FREECAD ASSEMBLY — COMPONENT RECIPES ("proj2")

This assembly document has 16 components, labeled P0..P15 below (a component is one placed body or linked part). 15 of them carry a construction recipe — the FreeCAD feature program that regenerates the part from scratch, quoted from this document or its linked companion documents; the rest are supplied as boundary geometry only. No exploded tour is included for this assembly.
COMPONENT P0 — geometry summary ("Assembly"; no construction recipe available for this part):
  bounding box: 60.6 x 47.8 x 42.0 mm
  tessellated surface: 6,332 triangles
  volume: 119726214130147568963238807791653928811536405446377303989115812334621021626623820741472012231102444157712454609502401804820784934384684739682024730656768 mm^3 (98328918981775611600278971227249126254820471256093482078634739637553224683712798080618531052465940639860308786772171943274562947930039704154529595392% of its bounding box)
COMPONENT P1 — recipe-attached ("classifier", modeled in this document).
Construction recipe (the document's own serialized feature program — sketch geometry with constraints, then the solid features built on it; lengths are millimeters unless a unit is written):

FEATURE [Sketcher::SketchObject] Sketch
  FullyConstrained = true
  MapMode = 5
  sketch-geometry (38):
    g0: LineSegment StartX=0 StartY=100 StartZ=0 EndX=0 EndY=200 EndZ=0
    g1: LineSegment StartX=0 StartY=200 StartZ=0 EndX=-86.6025 EndY=250 EndZ=0
    g2: LineSegment StartX=-86.6025 StartY=250 StartZ=0 EndX=-173.205 EndY=200 EndZ=0
    g3: LineSegment StartX=-173.205 StartY=200 StartZ=0 EndX=-173.205 EndY=100 EndZ=0
    g4: LineSegment StartX=-173.205 StartY=100 StartZ=0 EndX=-86.6025 EndY=50 EndZ=0
    g5: LineSegment StartX=-86.6025 StartY=50 StartZ=0 EndX=0 EndY=100 EndZ=0
    g6: Circle CenterX=-86.6025 CenterY=150 CenterZ=0 NormalX=0 NormalY=0 NormalZ=1 AngleXU=0 Radius=100
    g7: LineSegment StartX=173.205 StartY=100 StartZ=0 EndX=173.205 EndY=200 EndZ=0
    g8: LineSegment StartX=0 StartY=100 StartZ=0 EndX=86.6025 EndY=50 EndZ=0
    g9: LineSegment StartX=86.6025 StartY=50 StartZ=0 EndX=173.205 EndY=100 EndZ=0
    g10: LineSegment StartX=173.205 StartY=200 StartZ=0 EndX=86.6025 EndY=250 EndZ=0
    g11: LineSegment StartX=86.6025 StartY=250 StartZ=0 EndX=0 EndY=200 EndZ=0
    g12: Circle CenterX=86.6025 CenterY=150 CenterZ=0 NormalX=0 NormalY=0 NormalZ=1 AngleXU=0 Radius=100
    g13: LineSegment StartX=86.6025 StartY=-50 StartZ=0 EndX=86.6025 EndY=50 EndZ=0
    g14: LineSegment StartX=259.808 StartY=-50 StartZ=0 EndX=259.808 EndY=50 EndZ=0
    g15: LineSegment StartX=86.6025 StartY=-50 StartZ=0 EndX=173.205 EndY=-100 EndZ=0
    g16: LineSegment StartX=173.205 StartY=-100 StartZ=0 EndX=259.808 EndY=-50 EndZ=0
    g17: LineSegment StartX=259.808 StartY=50 StartZ=0 EndX=173.205 EndY=100 EndZ=0
    g18: Circle CenterX=173.205 CenterY=1e-16 CenterZ=0 NormalX=0 NormalY=0 NormalZ=1 AngleXU=0 Radius=100
    g19: LineSegment StartX=1.17e-14 StartY=-100 StartZ=0 EndX=86.6025 EndY=-50 EndZ=0
    g20: LineSegment StartX=86.6025 StartY=-250 StartZ=0 EndX=173.205 EndY=-200 EndZ=0
    g21: LineSegment StartX=1.76e-14 StartY=-200 StartZ=0 EndX=86.6025 EndY=-250 EndZ=0
    g22: LineSegment StartX=173.205 StartY=-200 StartZ=0 EndX=173.205 EndY=-100 EndZ=0
    g23: Circle CenterX=86.6025 CenterY=-150 CenterZ=0 NormalX=0 NormalY=0 NormalZ=1 AngleXU=0 Radius=100
    g24: LineSegment StartX=-86.6025 StartY=-50 StartZ=0 EndX=-86.6025 EndY=50 EndZ=0
    g25: LineSegment StartX=-173.205 StartY=100 StartZ=0 EndX=-259.808 EndY=50 EndZ=0
    g26: LineSegment StartX=-259.808 StartY=50 StartZ=0 EndX=-259.808 EndY=-50 EndZ=0
    g27: LineSegment StartX=-259.808 StartY=-50 StartZ=0 EndX=-173.205 EndY=-100 EndZ=0
    g28: LineSegment StartX=-173.205 StartY=-100 StartZ=0 EndX=-86.6025 EndY=-50 EndZ=0
    g29: Circle CenterX=-173.205 CenterY=-1.25e-14 CenterZ=0 NormalX=0 NormalY=0 NormalZ=1 AngleXU=0 Radius=100
    g30: LineSegment StartX=0 StartY=-200 StartZ=0 EndX=1.17e-14 EndY=-100 EndZ=0
    g31: LineSegment StartX=1.17e-14 StartY=-100 StartZ=0 EndX=-86.6025 EndY=-50 EndZ=0
    g32: LineSegment StartX=-173.205 StartY=-100 StartZ=0 EndX=-173.205 EndY=-200 EndZ=0
    g33: LineSegment StartX=-173.205 StartY=-200 StartZ=0 EndX=-86.6025 EndY=-250 EndZ=0
    g34: LineSegment StartX=-86.6025 StartY=-250 StartZ=0 EndX=0 EndY=-200 EndZ=0
    g35: Circle CenterX=-86.6025 CenterY=-150 CenterZ=0 NormalX=0 NormalY=0 NormalZ=1 AngleXU=0 Radius=100
    g36: GeomPoint X=86.6025 Y=150 Z=0
    g37: GeomPoint X=86.6025 Y=150 Z=0
  constraints (94):
    c: Coincident(g0,g1)
    c: Coincident(g1,g2)
    c: Coincident(g2,g3)
    c: Coincident(g3,g4)
    c: Coincident(g4,g5)
    c: Coincident(g5,g0)
    c: Equal(g0, g1-g5) x5
    c: PointOnObject(g0,g6)
    c: PointOnObject(g1,g6)
    c: PointOnObject(g2,g6)
    c: PointOnObject(g3,g6)
    c: PointOnObject(g4,g6)
    c: PointOnObject(g5,g6)
    c: Tangent(g0,g-2)
    c: DistanceY(g0,g0) = 100
    c: Coincident(g7,g10)
    c: Coincident(g10,g11)
    c: Coincident(g8,g9)
    c: Coincident(g9,g7)
    c: Equal(g7,g10)
    c: Equal(g7,g11)
    c: Equal(g7,g8)
    c: Equal(g7,g9)
    c: PointOnObject(g7,g12)
    c: PointOnObject(g10,g12)
    c: PointOnObject(g11,g12)
    c: PointOnObject(g8,g12)
    c: PointOnObject(g8,g12)
    c: PointOnObject(g9,g12)
    c: Equal(g0,g7) = 100
    c: Coincident(g11,g0)
    c: Coincident(g8,g0)
    c: Equal(g0,g13) = 100
    c: Coincident(g14,g17)
    c: Coincident(g15,g16)
    c: Coincident(g16,g14)
    c: Equal(g14,g17)
    c: Equal(g14,g15)
    c: Equal(g14,g16)
    c: PointOnObject(g14,g18)
    c: PointOnObject(g17,g18)
    c: PointOnObject(g13,g18)
    c: PointOnObject(g15,g18)
    c: PointOnObject(g15,g18)
    c: PointOnObject(g16,g18)
    c: Equal(g13,g14) = 100
    c: Coincident(g15,g13)
    c: Coincident(g17,g7)
    c: Coincident(g13,g8)
    c: Coincident(g20,g22)
    c: Coincident(g21,g20)
    c: Equal(g20,g22)
    c: Equal(g20,g21)
    c: PointOnObject(g20,g23)
    c: PointOnObject(g22,g23)
    c: PointOnObject(g19,g23)
    c: PointOnObject(g19,g23)
    c: PointOnObject(g21,g23)
    c: PointOnObject(g21,g23)
    c: Equal(g19,g20) = 100
    c: Coincident(g22,g15)
    c: Coincident(g19,g13)
    c: Equal(g22,g15)
    c: Coincident(g25,g26)
    c: Coincident(g26,g27)
    c: Coincident(g27,g28)
    c: Coincident(g28,g24)
    c: Equal(g24, g25-g28) x4
    c: PointOnObject(g24,g29)
    c: PointOnObject(g25,g29)
    c: PointOnObject(g25,g29)
    c: PointOnObject(g26,g29)
    c: PointOnObject(g27,g29)
    c: PointOnObject(g28,g29)
    c: Equal(g0,g24) = 100
    c: Coincident(g24,g4)
    c: Coincident(g25,g3)
    c: Coincident(g30,g31)
    c: Coincident(g32,g33)
    c: Coincident(g33,g34)
    c: Coincident(g34,g30)
    c: Equal(g30, g31-g34) x4
    c: PointOnObject(g30,g35)
    c: PointOnObject(g31,g35)
    c: PointOnObject(g32,g35)
    c: PointOnObject(g32,g35)
    c: PointOnObject(g33,g35)
    c: PointOnObject(g34,g35)
    c: Coincident(g31,g24)
    c: Coincident(g32,g27)
    c: Coincident(g19,g30)
    c: DistanceY(g-1,g8) = 50
    c: Coincident(g37,g36)
    c: Coincident(g36,g12)
FEATURE [PartDesign::Pad] Pad
  Direction = (0,0,1)
  Length = 200
  Length2 = 10
  Profile = -> Sketch
  ReferenceAxis = -> Sketch [N_Axis]
  Refine = true
  Type = 0
FEATURE [Sketcher::SketchObject] Sketch001
  ExternalGeometry = -> [Pad]
  FullyConstrained = true
  MapMode = 5
  Placement = pos=(0,0,200) rot=(0,0,1;0rad)
  sketch-geometry (42):
    g0: LineSegment StartX=168.875 StartY=102.5 StartZ=0 EndX=168.875 EndY=197.5 EndZ=0
    g1: LineSegment StartX=168.875 StartY=197.5 StartZ=0 EndX=86.6025 EndY=245 EndZ=0
    g2: LineSegment StartX=86.6025 StartY=245 StartZ=0 EndX=4.33013 EndY=197.5 EndZ=0
    g3: LineSegment StartX=4.33013 StartY=197.5 StartZ=0 EndX=4.33013 EndY=102.5 EndZ=0
    g4: LineSegment StartX=4.33013 StartY=102.5 StartZ=0 EndX=86.6025 EndY=55 EndZ=0
    g5: LineSegment StartX=86.6025 StartY=55 StartZ=0 EndX=168.875 EndY=102.5 EndZ=0
    g6: Circle CenterX=86.6025 CenterY=150 CenterZ=0 NormalX=0 NormalY=0 NormalZ=1 AngleXU=0 Radius=95
    g7: LineSegment StartX=173.205 StartY=95 StartZ=0 EndX=90.9327 EndY=47.5 EndZ=0
    g8: LineSegment StartX=255.477 StartY=47.5 StartZ=0 EndX=173.205 EndY=95 EndZ=0
    g9: LineSegment StartX=255.477 StartY=-47.5 StartZ=0 EndX=255.477 EndY=47.5 EndZ=0
    g10: LineSegment StartX=173.205 StartY=-95 StartZ=0 EndX=255.477 EndY=-47.5 EndZ=0
    g11: LineSegment StartX=90.9327 StartY=-47.5 StartZ=0 EndX=173.205 EndY=-95 EndZ=0
    g12: LineSegment StartX=90.9327 StartY=47.5 StartZ=0 EndX=90.9327 EndY=-47.5 EndZ=0
    g13: Circle CenterX=173.205 CenterY=0 CenterZ=0 NormalX=0 NormalY=0 NormalZ=1 AngleXU=0 Radius=95
    g14: LineSegment StartX=168.875 StartY=-102.5 StartZ=0 EndX=86.6025 EndY=-55 EndZ=0
    g15: LineSegment StartX=168.875 StartY=-197.5 StartZ=0 EndX=168.875 EndY=-102.5 EndZ=0
    g16: LineSegment StartX=86.6025 StartY=-245 StartZ=0 EndX=168.875 EndY=-197.5 EndZ=0
    g17: LineSegment StartX=4.33013 StartY=-197.5 StartZ=0 EndX=86.6025 EndY=-245 EndZ=0
    g18: LineSegment StartX=4.33013 StartY=-102.5 StartZ=0 EndX=4.33013 EndY=-197.5 EndZ=0
    g19: LineSegment StartX=86.6025 StartY=-55 StartZ=0 EndX=4.33013 EndY=-102.5 EndZ=0
    g20: Circle CenterX=86.6025 CenterY=-150 CenterZ=0 NormalX=0 NormalY=0 NormalZ=1 AngleXU=0 Radius=95
    g21: LineSegment StartX=-4.33013 StartY=-197.5 StartZ=0 EndX=-4.33013 EndY=-102.5 EndZ=0
    g22: LineSegment StartX=-4.33013 StartY=-102.5 StartZ=0 EndX=-86.6025 EndY=-55 EndZ=0
    g23: LineSegment StartX=-86.6025 StartY=-55 StartZ=0 EndX=-168.875 EndY=-102.5 EndZ=0
    g24: LineSegment StartX=-168.875 StartY=-102.5 StartZ=0 EndX=-168.875 EndY=-197.5 EndZ=0
    g25: LineSegment StartX=-168.875 StartY=-197.5 StartZ=0 EndX=-86.6025 EndY=-245 EndZ=0
    g26: LineSegment StartX=-86.6025 StartY=-245 StartZ=0 EndX=-4.33013 EndY=-197.5 EndZ=0
    g27: Circle CenterX=-86.6025 CenterY=-150 CenterZ=0 NormalX=0 NormalY=0 NormalZ=1 AngleXU=0 Radius=95
    g28: LineSegment StartX=-173.205 StartY=95 StartZ=0 EndX=-255.477 EndY=47.5 EndZ=0
    g29: LineSegment StartX=-90.9327 StartY=47.5 StartZ=0 EndX=-173.205 EndY=95 EndZ=0
    g30: LineSegment StartX=-90.9327 StartY=-47.5 StartZ=0 EndX=-90.9327 EndY=47.5 EndZ=0
    g31: LineSegment StartX=-173.205 StartY=-95 StartZ=0 EndX=-90.9327 EndY=-47.5 EndZ=0
    g32: LineSegment StartX=-255.477 StartY=-47.5 StartZ=0 EndX=-173.205 EndY=-95 EndZ=0
    g33: LineSegment StartX=-255.477 StartY=47.5 StartZ=0 EndX=-255.477 EndY=-47.5 EndZ=0
    g34: Circle CenterX=-173.205 CenterY=0 CenterZ=0 NormalX=0 NormalY=0 NormalZ=1 AngleXU=0 Radius=95
    g35: LineSegment StartX=-4.33013 StartY=197.5 StartZ=0 EndX=-86.6025 EndY=245 EndZ=0
    g36: LineSegment StartX=-86.6025 StartY=245 StartZ=0 EndX=-168.875 EndY=197.5 EndZ=0
    g37: LineSegment StartX=-4.33013 StartY=102.5 StartZ=0 EndX=-4.33013 EndY=197.5 EndZ=0
    g38: LineSegment StartX=-86.6025 StartY=55 StartZ=0 EndX=-4.33013 EndY=102.5 EndZ=0
    g39: LineSegment StartX=-168.875 StartY=102.5 StartZ=0 EndX=-86.6025 EndY=55 EndZ=0
    g40: LineSegment StartX=-168.875 StartY=197.5 StartZ=0 EndX=-168.875 EndY=102.5 EndZ=0
    g41: Circle CenterX=-86.6025 CenterY=150 CenterZ=0 NormalX=0 NormalY=0 NormalZ=1 AngleXU=0 Radius=95
  constraints (118):
    c: Coincident(g0,g1)
    c: Coincident(g1,g2)
    c: Coincident(g2,g3)
    c: Coincident(g3,g4)
    c: Coincident(g4,g5)
    c: Coincident(g5,g0)
    c: Equal(g0, g1-g5) x5
    c: PointOnObject(g0,g6)
    c: PointOnObject(g1,g6)
    c: PointOnObject(g2,g6)
    c: PointOnObject(g3,g6)
    c: PointOnObject(g4,g6)
    c: PointOnObject(g5,g6)
    c: Parallel(g0,g-4)
    c: Vertical(g1,g-20)
    c: PointOnObject(g0,g-5)
    c: DistanceY(g0,g0) = 95
    c: Coincident(g9,g8)
    c: Coincident(g8,g7)
    c: Coincident(g7,g12)
    c: Coincident(g12,g11)
    c: Coincident(g11,g10)
    c: Coincident(g10,g9)
    c: Equal(g9,g8)
    c: Equal(g9,g7)
    c: Equal(g9,g12)
    c: Equal(g9,g11)
    c: Equal(g9,g10)
    c: PointOnObject(g9,g13)
    c: PointOnObject(g8,g13)
    c: PointOnObject(g7,g13)
    c: PointOnObject(g12,g13)
    c: PointOnObject(g11,g13)
    c: PointOnObject(g10,g13)
    c: Equal(g0,g9) = 95
    c: Vertical(g7,g-5)
    c: Vertical(g-8,g10)
    c: PointOnObject(g13,g-1)
    c: Coincident(g15,g14)
    c: Coincident(g14,g19)
    c: Coincident(g19,g18)
    c: Coincident(g18,g17)
    c: Coincident(g17,g16)
    c: Coincident(g16,g15)
    c: Equal(g15,g14)
    c: Equal(g15,g19)
    c: Equal(g15,g18)
    c: Equal(g15,g17)
    c: Equal(g15,g16)
    c: PointOnObject(g15,g20)
    c: PointOnObject(g14,g20)
    c: PointOnObject(g19,g20)
    c: PointOnObject(g18,g20)
    c: PointOnObject(g17,g20)
    c: PointOnObject(g16,g20)
    c: PointOnObject(g14,g-7)
    c: PointOnObject(g17,g-11)
    c: Vertical(g16,g-10)
    c: DistanceY(g15,g15) = 95
    c: Coincident(g21,g22)
    c: Coincident(g22,g23)
    c: Coincident(g23,g24)
    c: Coincident(g24,g25)
    c: Coincident(g25,g26)
    c: Coincident(g26,g21)
    c: Equal(g21, g22-g26) x5
    c: PointOnObject(g21,g27)
    c: PointOnObject(g22,g27)
    c: PointOnObject(g23,g27)
    c: PointOnObject(g24,g27)
    c: PointOnObject(g25,g27)
    c: PointOnObject(g26,g27)
    c: Vertical(g25,g-12)
    c: PointOnObject(g21,g-10)
    c: PointOnObject(g23,g-14)
    c: DistanceY(g21,g21) = 95
    c: Coincident(g30,g29)
    c: Coincident(g29,g28)
    c: Coincident(g28,g33)
    c: Coincident(g33,g32)
    c: Coincident(g32,g31)
    c: Coincident(g31,g30)
    c: Equal(g30,g29)
    c: Equal(g30,g28)
    c: Equal(g30,g33)
    c: Equal(g30,g32)
    c: Equal(g30,g31)
    c: PointOnObject(g30,g34)
    c: PointOnObject(g29,g34)
    c: PointOnObject(g28,g34)
    c: PointOnObject(g33,g34)
    c: PointOnObject(g32,g34)
    c: PointOnObject(g31,g34)
    c: Equal(g21,g30) = 95
    c: PointOnObject(g34,g-1)
    c: Vertical(g28,g-17)
    c: Vertical(g31,g-14)
    c: Coincident(g37,g35)
    c: Coincident(g35,g36)
    c: Coincident(g36,g40)
    c: Coincident(g40,g39)
    c: Coincident(g39,g38)
    c: Coincident(g38,g37)
    c: Equal(g37,g35)
    c: Equal(g37,g36)
    c: Equal(g37,g40)
    c: Equal(g37,g39)
    c: Equal(g37,g38)
    c: PointOnObject(g37,g41)
    c: PointOnObject(g35,g41)
    c: PointOnObject(g36,g41)
    c: PointOnObject(g40,g41)
    c: PointOnObject(g39,g41)
    c: PointOnObject(g38,g41)
    c: Parallel(g35,g-19)
    c: Vertical(g35,g-19)
    c: PointOnObject(g35,g-20)
    c: DistanceY(g37,g37) = 95
FEATURE [PartDesign::Pocket] Pocket
  BaseFeature = -> Pad
  Direction = (0,0,-1)
  Length = 190
  Length2 = 5
  Profile = -> Sketch001
  ReferenceAxis = -> Sketch001 [N_Axis]
  Refine = true
  Type = 0
FEATURE [Sketcher::SketchObject] Sketch099
  FullyConstrained = true
  MapMode = 5
  Placement = pos=(90.9327,-1.36e-14,0) rot=(0.57735,0.57735,0.57735;2.0944rad)
  Support = -> [Pocket]
  sketch-geometry (2):
    g0: Circle CenterX=0 CenterY=15 CenterZ=0 NormalX=0 NormalY=0 NormalZ=1 AngleXU=0 Radius=3
    g1: Circle CenterX=0 CenterY=195 CenterZ=0 NormalX=0 NormalY=0 NormalZ=1 AngleXU=0 Radius=3
  constraints (6):
    c: PointOnObject(g0,g-2)
    c: Diameter(g0) = 6
    c: DistanceY(g-1,g0) = 15
    c: PointOnObject(g1,g-2)
    c: DistanceY(g-1,g1) = 195
    c: Equal(g1,g0)
FEATURE [PartDesign::Hole] Hole023
  BaseFeature = -> Pocket
  CustomThreadClearance = 0
  Depth = 25
  DepthType = 0
  Diameter = 2.52
  DrillForDepth = false
  DrillPoint = 1
  DrillPointAngle = 118
  HoleCutCountersinkAngle = 90
  HoleCutCustomValues = false
  HoleCutDepth = 0
  HoleCutDiameter = 6.1
  HoleCutType = 2
  ModelThread = true
  Profile = -> Sketch099
  Refine = true
  Tapered = false
  TaperedAngle = 90
  ThreadClass = 0
  ThreadDepth = 25
  ThreadDepthType = 0
  ThreadDirection = 0
  ThreadFit = 0
  ThreadSize = 9
  ThreadType = 1
  Threaded = true
  UseCustomThreadClearance = false
FEATURE [Sketcher::SketchObject] Sketch100
  FullyConstrained = true
  MapMode = 5
  Placement = pos=(-45.4663,78.75,0) rot=(-0.186157,0.694747,0.694747;3.50969rad)
  Support = -> [Hole023]
  sketch-geometry (2):
    g0: Circle CenterX=0 CenterY=15 CenterZ=0 NormalX=0 NormalY=0 NormalZ=1 AngleXU=0 Radius=3
    g1: Circle CenterX=0 CenterY=195 CenterZ=0 NormalX=0 NormalY=0 NormalZ=1 AngleXU=0 Radius=3
  constraints (6):
    c: PointOnObject(g0,g-2)
    c: Diameter(g0) = 6
    c: DistanceY(g-1,g0) = 15
    c: PointOnObject(g1,g-2)
    c: Diameter(g1) = 6
    c: DistanceY(g-1,g1) = 195
FEATURE [PartDesign::Hole] Hole024
  BaseFeature = -> Hole023
  CustomThreadClearance = 0
  Depth = 25
  DepthType = 0
  Diameter = 2.52
  DrillForDepth = false
  DrillPoint = 1
  DrillPointAngle = 118
  HoleCutCountersinkAngle = 90
  HoleCutCustomValues = false
  HoleCutDepth = 0
  HoleCutDiameter = 6.1
  HoleCutType = 2
  ModelThread = true
  Profile = -> Sketch100
  Refine = true
  Tapered = false
  TaperedAngle = 90
  ThreadClass = 0
  ThreadDepth = 25
  ThreadDepthType = 0
  ThreadDirection = 0
  ThreadFit = 0
  ThreadSize = 9
  ThreadType = 1
  Threaded = true
  UseCustomThreadClearance = false
FEATURE [Sketcher::SketchObject] Sketch101
  FullyConstrained = true
  MapMode = 5
  Placement = pos=(-45.4663,-78.75,0) rot=(0.935113,-0.250563,-0.250563;1.63783rad)
  Support = -> [Hole024]
  sketch-geometry (2):
    g0: Circle CenterX=0 CenterY=15 CenterZ=0 NormalX=0 NormalY=0 NormalZ=1 AngleXU=0 Radius=3
    g1: Circle CenterX=0 CenterY=195 CenterZ=0 NormalX=0 NormalY=0 NormalZ=1 AngleXU=0 Radius=3
  constraints (6):
    c: Diameter(g0) = 6
    c: PointOnObject(g0,g-2)
    c: DistanceY(g-1,g0) = 15
    c: PointOnObject(g1,g-2)
    c: Diameter(g1) = 6
    c: DistanceY(g-1,g1) = 195
FEATURE [PartDesign::Hole] Hole025
  BaseFeature = -> Hole024
  CustomThreadClearance = 0
  Depth = 25
  DepthType = 0
  Diameter = 2.52
  DrillForDepth = false
  DrillPoint = 1
  DrillPointAngle = 118
  HoleCutCountersinkAngle = 90
  HoleCutCustomValues = false
  HoleCutDepth = 0
  HoleCutDiameter = 6.1
  HoleCutType = 2
  ModelThread = true
  Profile = -> Sketch101
  Refine = true
  Tapered = false
  TaperedAngle = 90
  ThreadClass = 0
  ThreadDepth = 25
  ThreadDepthType = 0
  ThreadDirection = 0
  ThreadFit = 0
  ThreadSize = 9
  ThreadType = 1
  Threaded = true
  UseCustomThreadClearance = false
FEATURE [PartDesign::Body] Body  label="classifier"
  Group = -> [Sketch,Pad,Sketch001,Pocket,Sketch099,Hole023,Sketch100,Hole024,Sketch101,Hole025]
  Origin = -> Origin
  Placement = pos=(3,55,83.2) rot=(0,0,1;0rad)
  Tip = -> Hole025
COMPONENT P2 — recipe-attached ("semi_stationaryTop", modeled in this document).
Construction recipe (the document's own serialized feature program — sketch geometry with constraints, then the solid features built on it; lengths are millimeters unless a unit is written):

FEATURE [Sketcher::SketchObject] Sketch002
  FullyConstrained = true
  MapMode = 5
  sketch-geometry (7):
    g0: LineSegment StartX=86.6025 StartY=50 StartZ=0 EndX=-1.42e-14 EndY=100 EndZ=0
    g1: LineSegment StartX=-1.42e-14 StartY=100 StartZ=0 EndX=-86.6025 EndY=50 EndZ=0
    g2: LineSegment StartX=-86.6025 StartY=50 StartZ=0 EndX=-86.6025 EndY=-50 EndZ=0
    g3: LineSegment StartX=-86.6025 StartY=-50 StartZ=0 EndX=0 EndY=-100 EndZ=0
    g4: LineSegment StartX=0 StartY=-100 StartZ=0 EndX=86.6025 EndY=-50 EndZ=0
    g5: LineSegment StartX=86.6025 StartY=-50 StartZ=0 EndX=86.6025 EndY=50 EndZ=0
    g6: Circle CenterX=0 CenterY=0 CenterZ=0 NormalX=0 NormalY=0 NormalZ=1 AngleXU=0 Radius=100
  constraints (16):
    c: Coincident(g0,g1)
    c: Coincident(g1,g2)
    c: Coincident(g2,g3)
    c: Coincident(g3,g4)
    c: Coincident(g4,g5)
    c: Coincident(g5,g0)
    c: Equal(g0, g1-g5) x5
    c: PointOnObject(g0,g6)
    c: PointOnObject(g1,g6)
    c: PointOnObject(g2,g6)
    c: PointOnObject(g3,g6)
    c: PointOnObject(g4,g6)
    c: PointOnObject(g5,g6)
    c: Coincident(g6,g-1)
    c: PointOnObject(g3,g-2)
    c: DistanceY(g5,g5) = 100
FEATURE [PartDesign::Pad] Pad001
  Direction = (0,0,1)
  Length = 10
  Length2 = 10
  Profile = -> Sketch002
  ReferenceAxis = -> Sketch002 [N_Axis]
  Refine = true
  Type = 0
FEATURE [Sketcher::SketchObject] Sketch003  label="lock"
  FullyConstrained = true
  MapMode = 5
  Placement = pos=(0,0,10) rot=(0,0,1;0rad)
  sketch-geometry (1):
    g0: Circle CenterX=0 CenterY=0 CenterZ=0 NormalX=0 NormalY=0 NormalZ=1 AngleXU=0 Radius=15
  constraints (2):
    c: Coincident(g0,g-1)
    c: Diameter(g0) = 30
FEATURE [Sketcher::SketchObject] Sketch005  label="press_fit"
  FullyConstrained = true
  MapMode = 5
  Placement = pos=(0,0,0) rot=(1,0,0;3.14159rad)
  sketch-geometry (1):
    g0: Circle CenterX=0 CenterY=0 CenterZ=0 NormalX=0 NormalY=0 NormalZ=1 AngleXU=0 Radius=15.975
  constraints (2):
    c: Coincident(g0,g-1)
    c: Diameter(g0) = 31.95
FEATURE [PartDesign::Pocket] Pocket005
  BaseFeature = -> Pad001
  Direction = (0,1e-16,1)
  Length = 5
  Length2 = 5
  Profile = -> Sketch005
  ReferenceAxis = -> Sketch005 [N_Axis]
  Refine = true
  Type = 0
FEATURE [PartDesign::Pocket] Pocket006
  BaseFeature = -> Pocket005
  Direction = (0,0,-1)
  Length = 5
  Length2 = 5
  Profile = -> Sketch003
  ReferenceAxis = -> Sketch003 [N_Axis]
  Refine = true
  Type = 0
FEATURE [Sketcher::SketchObject] Sketch072
  FullyConstrained = true
  MapMode = 5
  Placement = pos=(0,0,10) rot=(0,0,1;0rad)
  Support = -> [Pocket006]
  sketch-geometry (7):
    g0: LineSegment StartX=35 StartY=-20.2073 StartZ=0 EndX=0 EndY=40.4145 EndZ=0
    g1: LineSegment StartX=0 StartY=40.4145 StartZ=0 EndX=-35 EndY=-20.2073 EndZ=0
    g2: LineSegment StartX=-35 StartY=-20.2073 StartZ=0 EndX=35 EndY=-20.2073 EndZ=0
    g3: Circle CenterX=0 CenterY=0 CenterZ=0 NormalX=0 NormalY=0 NormalZ=1 AngleXU=0 Radius=40.4145
    g4: Circle CenterX=0 CenterY=40.4145 CenterZ=0 NormalX=0 NormalY=0 NormalZ=1 AngleXU=0 Radius=3
    g5: Circle CenterX=35 CenterY=-20.2073 CenterZ=0 NormalX=0 NormalY=0 NormalZ=1 AngleXU=0 Radius=3
    g6: Circle CenterX=-35 CenterY=-20.2073 CenterZ=0 NormalX=0 NormalY=0 NormalZ=1 AngleXU=0 Radius=3
  constraints (17):
    c: Coincident(g0,g1)
    c: Coincident(g1,g2)
    c: Coincident(g2,g0)
    c: Equal(g0,g1)
    c: Equal(g0,g2)
    c: PointOnObject(g0,g3)
    c: PointOnObject(g1,g3)
    c: PointOnObject(g2,g3)
    c: Coincident(g3,g-1)
    c: PointOnObject(g0,g-2)
    c: DistanceX(g2,g2) = 70
    c: Coincident(g4,g0)
    c: Coincident(g5,g0)
    c: Coincident(g6,g1)
    c: Equal(g4,g6)
    c: Equal(g6,g5)
    c: Diameter(g4) = 6
FEATURE [PartDesign::Hole] Hole008
  BaseFeature = -> Pocket006
  CustomThreadClearance = 0
  Depth = 25
  DepthType = 0
  Diameter = 2.52
  DrillForDepth = false
  DrillPoint = 1
  DrillPointAngle = 118
  HoleCutCountersinkAngle = 90
  HoleCutCustomValues = false
  HoleCutDepth = 0
  HoleCutDiameter = 6.1
  HoleCutType = 2
  ModelThread = true
  Profile = -> Sketch072
  Refine = true
  Tapered = false
  TaperedAngle = 90
  ThreadClass = 0
  ThreadDepth = 25
  ThreadDepthType = 0
  ThreadDirection = 0
  ThreadFit = 0
  ThreadSize = 9
  ThreadType = 1
  Threaded = true
  UseCustomThreadClearance = false
FEATURE [Sketcher::SketchObject] Sketch083
  FullyConstrained = true
  MapMode = 5
  Placement = pos=(86.6025,-5.664e-13,0) rot=(0.57735,0.57735,0.57735;2.0944rad)
  Support = -> [Hole008]
  sketch-geometry (1):
    g0: Circle CenterX=0 CenterY=5 CenterZ=0 NormalX=0 NormalY=0 NormalZ=1 AngleXU=0 Radius=3
  constraints (3):
    c: PointOnObject(g0,g-2)
    c: Diameter(g0) = 6
    c: DistanceY(g-1,g0) = 5
FEATURE [PartDesign::Hole] Hole013
  BaseFeature = -> Hole008
  CustomThreadClearance = 0
  Depth = 15
  DepthType = 0
  Diameter = 2.52
  DrillForDepth = true
  DrillPoint = 1
  DrillPointAngle = 118
  HoleCutCountersinkAngle = 90
  HoleCutCustomValues = false
  HoleCutDepth = 0
  HoleCutDiameter = 6.1
  HoleCutType = 0
  ModelThread = true
  Profile = -> Sketch083
  Refine = true
  Tapered = false
  TaperedAngle = 90
  ThreadClass = 0
  ThreadDepth = 15
  ThreadDepthType = 0
  ThreadDirection = 0
  ThreadFit = 0
  ThreadSize = 9
  ThreadType = 1
  Threaded = true
  UseCustomThreadClearance = false
FEATURE [Sketcher::SketchObject] Sketch084
  FullyConstrained = true
  MapMode = 5
  Placement = pos=(-43.3013,75,0) rot=(-0.186157,0.694747,0.694747;3.50969rad)
  Support = -> [Hole013]
  sketch-geometry (1):
    g0: Circle CenterX=0 CenterY=5 CenterZ=0 NormalX=0 NormalY=0 NormalZ=1 AngleXU=0 Radius=3
  constraints (3):
    c: PointOnObject(g0,g-2)
    c: Diameter(g0) = 6
    c: DistanceY(g-1,g0) = 5
FEATURE [PartDesign::Hole] Hole014
  BaseFeature = -> Hole013
  CustomThreadClearance = 0
  Depth = 15
  DepthType = 0
  Diameter = 2.52
  DrillForDepth = true
  DrillPoint = 1
  DrillPointAngle = 118
  HoleCutCountersinkAngle = 90
  HoleCutCustomValues = false
  HoleCutDepth = 0
  HoleCutDiameter = 6.1
  HoleCutType = 0
  ModelThread = true
  Profile = -> Sketch084
  Refine = true
  Tapered = false
  TaperedAngle = 90
  ThreadClass = 0
  ThreadDepth = 15
  ThreadDepthType = 0
  ThreadDirection = 0
  ThreadFit = 0
  ThreadSize = 9
  ThreadType = 1
  Threaded = true
  UseCustomThreadClearance = false
FEATURE [Sketcher::SketchObject] Sketch085
  FullyConstrained = true
  MapMode = 5
  Placement = pos=(-43.3013,-75,0) rot=(0.935113,-0.250563,-0.250563;1.63783rad)
  Support = -> [Hole014]
  sketch-geometry (1):
    g0: Circle CenterX=0 CenterY=5 CenterZ=0 NormalX=0 NormalY=0 NormalZ=1 AngleXU=0 Radius=3
  constraints (3):
    c: PointOnObject(g0,g-2)
    c: Diameter(g0) = 6
    c: DistanceY(g-1,g0) = 5
FEATURE [PartDesign::Hole] Hole015
  BaseFeature = -> Hole014
  CustomThreadClearance = 0
  Depth = 15
  DepthType = 0
  Diameter = 2.52
  DrillForDepth = true
  DrillPoint = 1
  DrillPointAngle = 118
  HoleCutCountersinkAngle = 90
  HoleCutCustomValues = false
  HoleCutDepth = 0
  HoleCutDiameter = 6.1
  HoleCutType = 0
  ModelThread = true
  Profile = -> Sketch085
  Refine = true
  Tapered = false
  TaperedAngle = 90
  ThreadClass = 0
  ThreadDepth = 15
  ThreadDepthType = 0
  ThreadDirection = 0
  ThreadFit = 0
  ThreadSize = 9
  ThreadType = 1
  Threaded = true
  UseCustomThreadClearance = false
FEATURE [PartDesign::Body] Body001  label="semi_stationaryTop"
  Group = -> [Sketch002,Pad001,Sketch003,Sketch005,Pocket005,Pocket006,Sketch072,Hole008,Sketch083,Hole013,Sketch084,Hole014,Sketch085,Hole015]
  Origin = -> Origin001
  Placement = pos=(3.15,54.87,93.3) rot=(0,0,1;0rad)
  Tip = -> Hole015
COMPONENT P3 — recipe-attached ("semi_stationarybottom", modeled in this document).
Construction recipe (the document's own serialized feature program — sketch geometry with constraints, then the solid features built on it; lengths are millimeters unless a unit is written):

FEATURE [Sketcher::SketchObject] Sketch007
  FullyConstrained = true
  MapMode = 5
  sketch-geometry (7):
    g0: LineSegment StartX=86.6025 StartY=50 StartZ=0 EndX=-1.42e-14 EndY=100 EndZ=0
    g1: LineSegment StartX=-1.42e-14 StartY=100 StartZ=0 EndX=-86.6025 EndY=50 EndZ=0
    g2: LineSegment StartX=-86.6025 StartY=50 StartZ=0 EndX=-86.6025 EndY=-50 EndZ=0
    g3: LineSegment StartX=-86.6025 StartY=-50 StartZ=0 EndX=0 EndY=-100 EndZ=0
    g4: LineSegment StartX=0 StartY=-100 StartZ=0 EndX=86.6025 EndY=-50 EndZ=0
    g5: LineSegment StartX=86.6025 StartY=-50 StartZ=0 EndX=86.6025 EndY=50 EndZ=0
    g6: Circle CenterX=0 CenterY=0 CenterZ=0 NormalX=0 NormalY=0 NormalZ=1 AngleXU=0 Radius=100
  constraints (16):
    c: Coincident(g0,g1)
    c: Coincident(g1,g2)
    c: Coincident(g2,g3)
    c: Coincident(g3,g4)
    c: Coincident(g4,g5)
    c: Coincident(g5,g0)
    c: Equal(g0, g1-g5) x5
    c: PointOnObject(g0,g6)
    c: PointOnObject(g1,g6)
    c: PointOnObject(g2,g6)
    c: PointOnObject(g3,g6)
    c: PointOnObject(g4,g6)
    c: PointOnObject(g5,g6)
    c: Coincident(g6,g-1)
    c: PointOnObject(g3,g-2)
    c: DistanceY(g5,g5) = 100
FEATURE [PartDesign::Pad] Pad002
  Direction = (0,0,1)
  Length = 10
  Length2 = 10
  Profile = -> Sketch007
  ReferenceAxis = -> Sketch007 [N_Axis]
  Refine = true
  Type = 0
FEATURE [Sketcher::SketchObject] Sketch008  label="lock001"
  FullyConstrained = true
  MapMode = 5
  Placement = pos=(0,0,10) rot=(0,0,1;0rad)
  sketch-geometry (1):
    g0: Circle CenterX=0 CenterY=0 CenterZ=0 NormalX=0 NormalY=0 NormalZ=1 AngleXU=0 Radius=15
  constraints (2):
    c: Coincident(g0,g-1)
    c: Diameter(g0) = 30
FEATURE [Sketcher::SketchObject] Sketch009  label="press-fit"
  FullyConstrained = true
  MapMode = 5
  Placement = pos=(0,0,0) rot=(1,0,0;3.14159rad)
  sketch-geometry (1):
    g0: Circle CenterX=0 CenterY=0 CenterZ=0 NormalX=0 NormalY=0 NormalZ=1 AngleXU=0 Radius=15.975
  constraints (2):
    c: Coincident(g0,g-1)
    c: Diameter(g0) = 31.95
FEATURE [PartDesign::Pocket] Pocket007
  BaseFeature = -> Pad002
  Direction = (0,0,1)
  Length = 5
  Length2 = 5
  Profile = -> Sketch009
  ReferenceAxis = -> Sketch009 [N_Axis]
  Refine = true
  Type = 0
FEATURE [PartDesign::Pocket] Pocket008
  BaseFeature = -> Pocket007
  Direction = (0,0,-1)
  Length = 5
  Length2 = 5
  Profile = -> Sketch008
  ReferenceAxis = -> Sketch008 [N_Axis]
  Refine = true
  Type = 0
FEATURE [Sketcher::SketchObject] Sketch024
  FullyConstrained = true
  MapMode = 5
  Placement = pos=(0,0,10) rot=(0,0,1;0rad)
  sketch-geometry (7):
    g0: LineSegment StartX=35 StartY=-20.2073 StartZ=0 EndX=0 EndY=40.4145 EndZ=0
    g1: LineSegment StartX=0 StartY=40.4145 StartZ=0 EndX=-35 EndY=-20.2073 EndZ=0
    g2: LineSegment StartX=-35 StartY=-20.2073 StartZ=0 EndX=35 EndY=-20.2073 EndZ=0
    g3: Circle CenterX=0 CenterY=0 CenterZ=0 NormalX=0 NormalY=0 NormalZ=1 AngleXU=0 Radius=40.4145
    g4: Circle CenterX=35 CenterY=-20.2073 CenterZ=0 NormalX=0 NormalY=0 NormalZ=1 AngleXU=0 Radius=3
    g5: Circle CenterX=0 CenterY=40.4145 CenterZ=0 NormalX=0 NormalY=0 NormalZ=1 AngleXU=0 Radius=3
    g6: Circle CenterX=-35 CenterY=-20.2073 CenterZ=0 NormalX=0 NormalY=0 NormalZ=1 AngleXU=0 Radius=3
  constraints (17):
    c: Coincident(g0,g1)
    c: Coincident(g1,g2)
    c: Coincident(g2,g0)
    c: Equal(g0,g1)
    c: Equal(g0,g2)
    c: PointOnObject(g0,g3)
    c: PointOnObject(g1,g3)
    c: PointOnObject(g2,g3)
    c: Coincident(g3,g-1)
    c: PointOnObject(g0,g-2)
    c: DistanceX(g2,g2) = 70
    c: Coincident(g4,g0)
    c: Diameter(g4) = 6
    c: Coincident(g5,g0)
    c: Coincident(g6,g1)
    c: Equal(g6,g5)
    c: Equal(g5,g4)
FEATURE [PartDesign::Hole] Hole004
  BaseFeature = -> Pocket008
  CustomThreadClearance = 0
  Depth = 7
  DepthType = 0
  Diameter = 2.52
  DrillForDepth = true
  DrillPoint = 1
  DrillPointAngle = 118
  HoleCutCountersinkAngle = 90
  HoleCutCustomValues = false
  HoleCutDepth = 0
  HoleCutDiameter = 6.1
  HoleCutType = 0
  ModelThread = true
  Profile = -> Sketch024
  Refine = true
  Tapered = false
  TaperedAngle = 90
  ThreadClass = 0
  ThreadDepth = 7
  ThreadDepthType = 0
  ThreadDirection = 0
  ThreadFit = 0
  ThreadSize = 9
  ThreadType = 1
  Threaded = true
  UseCustomThreadClearance = false
FEATURE [Sketcher::SketchObject] Sketch066
  FullyConstrained = true
  MapMode = 5
  Placement = pos=(0,0,0) rot=(1,0,0;3.14159rad)
  Support = -> [Hole004]
  sketch-geometry (7):
    g0: LineSegment StartX=35 StartY=-20.2073 StartZ=0 EndX=0 EndY=40.4145 EndZ=0
    g1: LineSegment StartX=0 StartY=40.4145 StartZ=0 EndX=-35 EndY=-20.2073 EndZ=0
    g2: LineSegment StartX=-35 StartY=-20.2073 StartZ=0 EndX=35 EndY=-20.2073 EndZ=0
    g3: Circle CenterX=0 CenterY=0 CenterZ=0 NormalX=0 NormalY=0 NormalZ=1 AngleXU=0 Radius=40.4145
    g4: Circle CenterX=35 CenterY=-20.2073 CenterZ=0 NormalX=0 NormalY=0 NormalZ=1 AngleXU=0 Radius=3
    g5: Circle CenterX=0 CenterY=40.4145 CenterZ=0 NormalX=0 NormalY=0 NormalZ=1 AngleXU=0 Radius=3
    g6: Circle CenterX=-35 CenterY=-20.2073 CenterZ=0 NormalX=0 NormalY=0 NormalZ=1 AngleXU=0 Radius=3
  constraints (17):
    c: Coincident(g0,g1)
    c: Coincident(g1,g2)
    c: Coincident(g2,g0)
    c: Equal(g0,g1)
    c: Equal(g0,g2)
    c: PointOnObject(g0,g3)
    c: PointOnObject(g1,g3)
    c: PointOnObject(g2,g3)
    c: Coincident(g3,g-1)
    c: PointOnObject(g0,g-2)
    c: DistanceX(g2,g2) = 70
    c: Coincident(g4,g0)
    c: Coincident(g5,g0)
    c: Coincident(g6,g1)
    c: Equal(g6,g4)
    c: Equal(g4,g5)
    c: Diameter(g5) = 6
FEATURE [PartDesign::Hole] Hole005
  BaseFeature = -> Hole004
  CustomThreadClearance = 0
  Depth = 7
  DepthType = 0
  Diameter = 2.52
  DrillForDepth = true
  DrillPoint = 1
  DrillPointAngle = 118
  HoleCutCountersinkAngle = 90
  HoleCutCustomValues = false
  HoleCutDepth = 0
  HoleCutDiameter = 6.1
  HoleCutType = 0
  ModelThread = true
  Profile = -> Sketch066
  Refine = true
  Tapered = false
  TaperedAngle = 90
  ThreadClass = 0
  ThreadDepth = 7
  ThreadDepthType = 0
  ThreadDirection = 0
  ThreadFit = 0
  ThreadSize = 9
  ThreadType = 1
  Threaded = true
  UseCustomThreadClearance = false
FEATURE [Sketcher::SketchObject] Sketch070
  FullyConstrained = false
  MapMode = 5
  Placement = pos=(0,0,0) rot=(1,0,0;3.14159rad)
  Support = -> [Hole005]
  sketch-geometry (7):
    g0: LineSegment StartX=35 StartY=20.2073 StartZ=0 EndX=-35 EndY=20.2073 EndZ=0
    g1: LineSegment StartX=-35 StartY=20.2073 StartZ=0 EndX=0 EndY=-40.4145 EndZ=0
    g2: LineSegment StartX=0 StartY=-40.4145 StartZ=0 EndX=35 EndY=20.2073 EndZ=0
    g3: Circle CenterX=0 CenterY=0 CenterZ=0 NormalX=0 NormalY=0 NormalZ=1 AngleXU=0 Radius=40.4145
    g4: Circle CenterX=-35 CenterY=20.2073 CenterZ=0 NormalX=0 NormalY=0 NormalZ=1 AngleXU=0 Radius=3.38129
    g5: Circle CenterX=35 CenterY=20.2073 CenterZ=0 NormalX=0 NormalY=0 NormalZ=1 AngleXU=0 Radius=3.38129
    g6: Circle CenterX=0 CenterY=-40.4145 CenterZ=0 NormalX=0 NormalY=0 NormalZ=1 AngleXU=0 Radius=3.38129
  constraints (16):
    c: Coincident(g0,g1)
    c: Coincident(g1,g2)
    c: Coincident(g2,g0)
    c: Equal(g0,g1)
    c: Equal(g0,g2)
    c: PointOnObject(g0,g3)
    c: PointOnObject(g1,g3)
    c: PointOnObject(g2,g3)
    c: PointOnObject(g1,g-2)
    c: DistanceX(g0,g0) = 70
    c: Coincident(g3,g-1)
    c: Coincident(g4,g0)
    c: Coincident(g5,g0)
    c: Coincident(g6,g1)
    c: Equal(g6,g5)
    c: Equal(g5,g4)
FEATURE [PartDesign::Hole] Hole007
  BaseFeature = -> Hole005
  CustomThreadClearance = 0
  Depth = 7
  DepthType = 0
  Diameter = 2.52
  DrillForDepth = true
  DrillPoint = 1
  DrillPointAngle = 118
  HoleCutCountersinkAngle = 90
  HoleCutCustomValues = false
  HoleCutDepth = 0
  HoleCutDiameter = 6.1
  HoleCutType = 0
  ModelThread = true
  Profile = -> Sketch070
  Refine = true
  Tapered = false
  TaperedAngle = 90
  ThreadClass = 0
  ThreadDepth = 7
  ThreadDepthType = 0
  ThreadDirection = 0
  ThreadFit = 0
  ThreadSize = 9
  ThreadType = 1
  Threaded = true
  UseCustomThreadClearance = false
FEATURE [PartDesign::Body] Body002  label="semi_stationarybottom"
  Group = -> [Sketch007,Pad002,Sketch008,Sketch009,Pocket007,Pocket008,Sketch024,Hole004,Sketch066,Hole005,Sketch070,Hole007]
  Origin = -> Origin002
  Placement = pos=(3.1,54.8,93.3) rot=(1,0,0;3.14159rad)
  Tip = -> Hole007
COMPONENT P4 — recipe-attached ("gear66", modeled in this document).
Construction recipe (the document's own serialized feature program — sketch geometry with constraints, then the solid features built on it; lengths are millimeters unless a unit is written):

FEATURE [PartDesign::FeaturePython] TimingGear  label="TimingGear66"  # WARN: FeaturePython — macro-defined, semantics opaque (R4)
  AttacherType = Attacher::AttachEngine3D
  h = 0.75
  height = 6
  num_teeth = 66
  offset = 0.4
  pitch = 2
  r0 = 0.555
  r1 = 1
  rs = 0.15
  type = 0
  u = 0.254
  version = 1.3.0
FEATURE [Sketcher::SketchObject] Sketch020
  FullyConstrained = true
  MapMode = 5
  Placement = pos=(0,0,6) rot=(0,0,1;0rad)
  sketch-geometry (1):
    g0: Circle CenterX=0 CenterY=0 CenterZ=0 NormalX=0 NormalY=0 NormalZ=1 AngleXU=0 Radius=17.5
  constraints (2):
    c: Coincident(g0,g-1)
    c: Diameter(g0) = 35
FEATURE [Sketcher::SketchObject] Sketch023
  FullyConstrained = true
  MapMode = 5
  Placement = pos=(0,0,0) rot=(1,0,0;3.14159rad)
  sketch-geometry (1):
    g0: Circle CenterX=0 CenterY=0 CenterZ=0 NormalX=0 NormalY=0 NormalZ=1 AngleXU=0 Radius=12.5
  constraints (2):
    c: Coincident(g0,g-1)
    c: Diameter(g0) = 25
FEATURE [PartDesign::Pocket] Pocket009
  BaseFeature = -> TimingGear
  Direction = (0,0,1)
  Length = 30
  Length2 = 5
  Profile = -> Sketch023
  ReferenceAxis = -> Sketch023 [N_Axis]
  Refine = true
  Type = 0
FEATURE [PartDesign::Pad] Pad014
  BaseFeature = -> Pocket009
  Direction = (0,0,1)
  Length = 0.5
  Length2 = 10
  Profile = -> Sketch020
  ReferenceAxis = -> Sketch020 [N_Axis]
  Refine = true
  Type = 0
FEATURE [Sketcher::SketchObject] Sketch028
  FullyConstrained = true
  MapMode = 5
  Placement = pos=(0,0,6.5) rot=(0,0,1;0rad)
  Support = -> [Pad014]
  sketch-geometry (1):
    g0: Circle CenterX=0 CenterY=0 CenterZ=0 NormalX=0 NormalY=0 NormalZ=1 AngleXU=0 Radius=22.5
  constraints (2):
    c: Coincident(g0,g-1)
    c: Diameter(g0) = 45
FEATURE [PartDesign::Pad] Pad015
  BaseFeature = -> Pad014
  Direction = (0,0,1)
  Length = 10
  Length2 = 10
  Profile = -> Sketch028
  ReferenceAxis = -> Sketch028 [N_Axis]
  Refine = true
  Type = 0
FEATURE [Sketcher::SketchObject] Sketch021
  FullyConstrained = true
  MapMode = 5
  Placement = pos=(0,0,16.5) rot=(0,0,1;0rad)
  Support = -> [Pad015]
  sketch-geometry (1):
    g0: Circle CenterX=0 CenterY=0 CenterZ=0 NormalX=0 NormalY=0 NormalZ=1 AngleXU=0 Radius=50
  constraints (2):
    c: Coincident(g0,g-1)
    c: Diameter(g0) = 100
FEATURE [PartDesign::Pad] Pad016
  BaseFeature = -> Pad015
  Direction = (0,0,1)
  Length = 10
  Length2 = 10
  Profile = -> Sketch021
  ReferenceAxis = -> Sketch021 [N_Axis]
  Refine = true
  Type = 0
FEATURE [Sketcher::SketchObject] Sketch022
  FullyConstrained = true
  MapMode = 5
  Placement = pos=(0,0,16.5) rot=(1,0,0;3.14159rad)
  Support = -> [Pad016]
  sketch-geometry (7):
    g0: LineSegment StartX=35 StartY=-20.2073 StartZ=0 EndX=0 EndY=40.4145 EndZ=0
    g1: LineSegment StartX=0 StartY=40.4145 StartZ=0 EndX=-35 EndY=-20.2073 EndZ=0
    g2: LineSegment StartX=-35 StartY=-20.2073 StartZ=0 EndX=35 EndY=-20.2073 EndZ=0
    g3: Circle CenterX=0 CenterY=0 CenterZ=0 NormalX=0 NormalY=0 NormalZ=1 AngleXU=0 Radius=40.4145
    g4: Circle CenterX=0 CenterY=40.4145 CenterZ=0 NormalX=0 NormalY=0 NormalZ=1 AngleXU=0 Radius=2
    g5: Circle CenterX=35 CenterY=-20.2073 CenterZ=0 NormalX=0 NormalY=0 NormalZ=1 AngleXU=0 Radius=2
    g6: Circle CenterX=-35 CenterY=-20.2073 CenterZ=0 NormalX=0 NormalY=0 NormalZ=1 AngleXU=0 Radius=2
  constraints (17):
    c: Coincident(g0,g1)
    c: Coincident(g1,g2)
    c: Coincident(g2,g0)
    c: Equal(g0,g1)
    c: Equal(g0,g2)
    c: PointOnObject(g0,g3)
    c: PointOnObject(g1,g3)
    c: PointOnObject(g2,g3)
    c: Coincident(g3,g-1)
    c: PointOnObject(g0,g-2)
    c: Coincident(g4,g0)
    c: DistanceX(g2,g2) = 70
    c: Coincident(g5,g0)
    c: Coincident(g6,g1)
    c: Equal(g6,g4)
    c: Equal(g4,g5)
    c: Diameter(g6) = 4
FEATURE [Sketcher::SketchObject] Sketch065
  FullyConstrained = true
  MapMode = 5
  Placement = pos=(0,0,26.5) rot=(0,0,1;0rad)
  Support = -> [Pad016]
  sketch-geometry (1):
    g0: Circle CenterX=0 CenterY=0 CenterZ=0 NormalX=0 NormalY=0 NormalZ=1 AngleXU=0 Radius=12.5
  constraints (2):
    c: Coincident(g0,g-1)
    c: Diameter(g0) = 25
FEATURE [PartDesign::Pocket] Pocket016
  BaseFeature = -> Pad016
  Direction = (0,0,-1)
  Length = 30
  Length2 = 5
  Profile = -> Sketch065
  ReferenceAxis = -> Sketch065 [N_Axis]
  Refine = true
  Type = 0
FEATURE [PartDesign::Hole] Hole003
  BaseFeature = -> Pocket016
  CustomThreadClearance = 0
  Depth = 25
  DepthType = 0
  Diameter = 2.52
  DrillForDepth = false
  DrillPoint = 1
  DrillPointAngle = 118
  HoleCutCountersinkAngle = 90
  HoleCutCustomValues = false
  HoleCutDepth = 0
  HoleCutDiameter = 6.1
  HoleCutType = 2
  ModelThread = true
  Profile = -> Sketch022
  Refine = true
  Tapered = false
  TaperedAngle = 90
  ThreadClass = 0
  ThreadDepth = 25
  ThreadDepthType = 0
  ThreadDirection = 0
  ThreadFit = 0
  ThreadSize = 9
  ThreadType = 1
  Threaded = true
  UseCustomThreadClearance = false
FEATURE [PartDesign::Body] Body003  label="gear66"
  Group = -> [TimingGear,Sketch020,Sketch021,Sketch022,Sketch023,Pocket009,Pad014,Sketch028,Pad015,Pad016,Sketch065,Pocket016,Hole003]
  Origin = -> Origin003
  Placement = pos=(2.95,54.95,56.75) rot=(0,0,1;0rad)
  Tip = -> Hole003
COMPONENT P5 — recipe-attached ("gear60", modeled in this document).
Construction recipe (the document's own serialized feature program — sketch geometry with constraints, then the solid features built on it; lengths are millimeters unless a unit is written):

FEATURE [PartDesign::FeaturePython] TimingGear001  # WARN: FeaturePython — macro-defined, semantics opaque (R4)
  AttacherType = Attacher::AttachEngine3D
  h = 0.75
  height = 6
  num_teeth = 60
  offset = 0.4
  pitch = 2
  r0 = 0.555
  r1 = 1
  rs = 0.15
  type = 0
  u = 0.254
  version = 1.3.0
FEATURE [Sketcher::SketchObject] Sketch012
  FullyConstrained = true
  MapMode = 5
  Placement = pos=(0,0,6) rot=(0,0,1;0rad)
  sketch-geometry (1):
    g0: Circle CenterX=0 CenterY=0 CenterZ=0 NormalX=0 NormalY=0 NormalZ=1 AngleXU=0 Radius=17.5
  constraints (2):
    c: Coincident(g0,g-1)
    c: Diameter(g0) = 35
FEATURE [PartDesign::Pad] Pad003
  BaseFeature = -> TimingGear001
  Direction = (0,0,1)
  Length = 0.5
  Length2 = 10
  Profile = -> Sketch012
  ReferenceAxis = -> Sketch012 [N_Axis]
  Refine = true
  Type = 0
FEATURE [Sketcher::SketchObject] Sketch013
  FullyConstrained = true
  MapMode = 5
  Placement = pos=(0,0,6.5) rot=(0,0,1;0rad)
  sketch-geometry (1):
    g0: Circle CenterX=0 CenterY=0 CenterZ=0 NormalX=0 NormalY=0 NormalZ=1 AngleXU=0 Radius=21
  constraints (2):
    c: Coincident(g0,g-1)
    c: Diameter(g0) = 42
FEATURE [PartDesign::Pad] Pad004
  BaseFeature = -> Pad003
  Direction = (0,0,1)
  Length = 2
  Length2 = 10
  Profile = -> Sketch013
  ReferenceAxis = -> Sketch013 [N_Axis]
  Refine = true
  Type = 0
FEATURE [Sketcher::SketchObject] Sketch014
  FullyConstrained = true
  MapMode = 5
  Placement = pos=(0,0,8.5) rot=(0,0,1;0rad)
  sketch-geometry (1):
    g0: Circle CenterX=0 CenterY=0 CenterZ=0 NormalX=0 NormalY=0 NormalZ=1 AngleXU=0 Radius=17.5
  constraints (2):
    c: Coincident(g0,g-1)
    c: Diameter(g0) = 35
FEATURE [PartDesign::Pad] Pad005
  BaseFeature = -> Pad004
  Direction = (0,0,1)
  Length = 0.5
  Length2 = 10
  Profile = -> Sketch014
  ReferenceAxis = -> Sketch014 [N_Axis]
  Refine = true
  Type = 0
FEATURE [Sketcher::SketchObject] Sketch015
  FullyConstrained = true
  MapMode = 5
  Placement = pos=(0,0,9) rot=(0,0,1;0rad)
  sketch-geometry (1):
    g0: Circle CenterX=0 CenterY=0 CenterZ=0 NormalX=0 NormalY=0 NormalZ=1 AngleXU=0 Radius=21
  constraints (2):
    c: Coincident(g0,g-1)
    c: Diameter(g0) = 42
FEATURE [PartDesign::Pad] Pad006
  BaseFeature = -> Pad005
  Direction = (0,0,1)
  Length = 2
  Length2 = 10
  Profile = -> Sketch015
  ReferenceAxis = -> Sketch015 [N_Axis]
  Refine = true
  Type = 0
FEATURE [PartDesign::Fillet] Fillet001
  Base = -> Pad006 [Edge1087,Edge1089,Edge4,Edge6]
  BaseFeature = -> Pad006
  Radius = 0.2
  Refine = true
  SupportTransform = false
  UseAllEdges = false
FEATURE [Sketcher::SketchObject] Sketch052
  FullyConstrained = true
  MapMode = 5
  Placement = pos=(0,0,0) rot=(1,0,0;3.14159rad)
  Support = -> [Fillet001]
  sketch-geometry (1):
    g0: Circle CenterX=0 CenterY=0 CenterZ=0 NormalX=0 NormalY=0 NormalZ=1 AngleXU=0 Radius=17.5
  constraints (2):
    c: Coincident(g0,g-1)
    c: Diameter(g0) = 35
FEATURE [PartDesign::Pad] Pad031
  BaseFeature = -> Fillet001
  Direction = (0,0,-1)
  Length = 0.5
  Length2 = 10
  Profile = -> Sketch052
  ReferenceAxis = -> Sketch052 [N_Axis]
  Refine = true
  Type = 0
FEATURE [Sketcher::SketchObject] Sketch053
  FullyConstrained = true
  MapMode = 5
  Placement = pos=(0,0,-0.5) rot=(1,0,0;3.14159rad)
  Support = -> [Pad031]
  sketch-geometry (1):
    g0: Circle CenterX=0 CenterY=0 CenterZ=0 NormalX=0 NormalY=0 NormalZ=1 AngleXU=0 Radius=21
  constraints (2):
    c: Coincident(g0,g-1)
    c: Diameter(g0) = 42
FEATURE [PartDesign::Pad] Pad032
  BaseFeature = -> Pad031
  Direction = (0,0,-1)
  Length = 2
  Length2 = 10
  Profile = -> Sketch053
  ReferenceAxis = -> Sketch053 [N_Axis]
  Refine = true
  Type = 0
FEATURE [Sketcher::SketchObject] Sketch054
  FullyConstrained = true
  MapMode = 5
  Placement = pos=(0,0,-2.5) rot=(1,0,0;3.14159rad)
  Support = -> [Pad032]
  sketch-geometry (1):
    g0: Circle CenterX=0 CenterY=0 CenterZ=0 NormalX=0 NormalY=0 NormalZ=1 AngleXU=0 Radius=2.55
  constraints (2):
    c: Coincident(g0,g-1)
    c: Diameter(g0) = 5.1
FEATURE [PartDesign::Pocket] Pocket014
  BaseFeature = -> Pad032
  Direction = (0,0,1)
  Length = 20
  Length2 = 5
  Profile = -> Sketch054
  ReferenceAxis = -> Sketch054 [N_Axis]
  Refine = true
  Type = 0
FEATURE [Sketcher::SketchObject] Sketch063
  FullyConstrained = true
  MapMode = 5
  Placement = pos=(0,0,11) rot=(0,0,1;0rad)
  Support = -> [Pocket014]
  sketch-geometry (7):
    g0: LineSegment StartX=10 StartY=-5.7735 StartZ=0 EndX=0 EndY=11.547 EndZ=0
    g1: LineSegment StartX=0 StartY=11.547 StartZ=0 EndX=-10 EndY=-5.7735 EndZ=0
    g2: LineSegment StartX=-10 StartY=-5.7735 StartZ=0 EndX=10 EndY=-5.7735 EndZ=0
    g3: Circle CenterX=0 CenterY=0 CenterZ=0 NormalX=0 NormalY=0 NormalZ=1 AngleXU=0 Radius=11.547
    g4: Circle CenterX=0 CenterY=11.547 CenterZ=0 NormalX=0 NormalY=0 NormalZ=1 AngleXU=0 Radius=2.8
    g5: Circle CenterX=10 CenterY=-5.7735 CenterZ=0 NormalX=0 NormalY=0 NormalZ=1 AngleXU=0 Radius=2.8
    g6: Circle CenterX=-10 CenterY=-5.7735 CenterZ=0 NormalX=0 NormalY=0 NormalZ=1 AngleXU=0 Radius=2.8
  constraints (17):
    c: Coincident(g0,g1)
    c: Coincident(g1,g2)
    c: Coincident(g2,g0)
    c: Equal(g0,g1)
    c: Equal(g0,g2)
    c: PointOnObject(g0,g3)
    c: PointOnObject(g1,g3)
    c: PointOnObject(g2,g3)
    c: Coincident(g3,g-1)
    c: PointOnObject(g0,g-2)
    c: Coincident(g4,g0)
    c: Coincident(g5,g0)
    c: Coincident(g6,g1)
    c: Equal(g5,g4)
    c: Equal(g4,g6)
    c: Diameter(g5) = 5.6
    c: DistanceX(g2,g2) = 20
FEATURE [PartDesign::Hole] Hole
  BaseFeature = -> Pocket014
  CustomThreadClearance = 0
  Depth = 6
  DepthType = 0
  Diameter = 2.52
  DrillForDepth = true
  DrillPoint = 1
  DrillPointAngle = 118
  HoleCutCountersinkAngle = 90
  HoleCutCustomValues = false
  HoleCutDepth = 0
  HoleCutDiameter = 6.1
  HoleCutType = 0
  ModelThread = true
  Profile = -> Sketch063
  Refine = true
  Tapered = false
  TaperedAngle = 90
  ThreadClass = 0
  ThreadDepth = 6
  ThreadDepthType = 0
  ThreadDirection = 0
  ThreadFit = 0
  ThreadSize = 9
  ThreadType = 1
  Threaded = true
  UseCustomThreadClearance = false
FEATURE [PartDesign::Body] Body004  label="gear60"
  Group = -> [TimingGear001,Sketch012,Pad003,Sketch013,Pad004,Sketch014,Pad005,Sketch015,Pad006,Fillet001,Sketch052,Pad031,Sketch053,Pad032,Sketch054,Pocket014,Sketch063,Hole]
  Origin = -> Origin004
  Placement = pos=(-45,3,45.25) rot=(0,0,1;0rad)
  Tip = -> Hole
COMPONENT P6 — recipe-attached ("gear20", modeled in this document).
Construction recipe (the document's own serialized feature program — sketch geometry with constraints, then the solid features built on it; lengths are millimeters unless a unit is written):

FEATURE [PartDesign::FeaturePython] TimingGear002  # WARN: FeaturePython — macro-defined, semantics opaque (R4)
  AttacherType = Attacher::AttachEngine3D
  h = 0.75
  height = 6
  num_teeth = 20
  offset = 0.4
  pitch = 2
  r0 = 0.555
  r1 = 1
  rs = 0.15
  type = 0
  u = 0.254
  version = 1.3.0
FEATURE [Sketcher::SketchObject] Sketch046
  FullyConstrained = true
  MapMode = 5
  Support = -> [XY_Plane005]
FEATURE [Sketcher::SketchObject] Sketch047
  FullyConstrained = true
  MapMode = 5
  Placement = pos=(0,0,6) rot=(0,0,1;0rad)
  Support = -> [TimingGear002]
  sketch-geometry (1):
    g0: Circle CenterX=0 CenterY=0 CenterZ=0 NormalX=0 NormalY=0 NormalZ=1 AngleXU=0 Radius=5
  constraints (2):
    c: Coincident(g0,g-1)
    c: Diameter(g0) = 10
FEATURE [PartDesign::Pad] Pad027
  BaseFeature = -> TimingGear002
  Direction = (0,0,1)
  Length = 0.5
  Length2 = 10
  Profile = -> Sketch047
  ReferenceAxis = -> Sketch047 [N_Axis]
  Refine = true
  Type = 0
FEATURE [Sketcher::SketchObject] Sketch048
  FullyConstrained = true
  MapMode = 5
  Placement = pos=(0,0,6.5) rot=(0,0,1;0rad)
  Support = -> [Pad027]
  sketch-geometry (1):
    g0: Circle CenterX=0 CenterY=0 CenterZ=0 NormalX=0 NormalY=0 NormalZ=1 AngleXU=0 Radius=10
  constraints (2):
    c: Coincident(g0,g-1)
    c: Diameter(g0) = 20
FEATURE [PartDesign::Pad] Pad028
  BaseFeature = -> Pad027
  Direction = (0,0,1)
  Length = 2
  Length2 = 10
  Profile = -> Sketch048
  ReferenceAxis = -> Sketch048 [N_Axis]
  Refine = true
  Type = 0
FEATURE [Sketcher::SketchObject] Sketch049
  FullyConstrained = true
  MapMode = 5
  Placement = pos=(0,0,0) rot=(1,0,0;3.14159rad)
  Support = -> [Pad028]
  sketch-geometry (1):
    g0: Circle CenterX=0 CenterY=0 CenterZ=0 NormalX=0 NormalY=0 NormalZ=1 AngleXU=0 Radius=5
  constraints (2):
    c: Coincident(g0,g-1)
    c: Diameter(g0) = 10
FEATURE [PartDesign::Pad] Pad029
  BaseFeature = -> Pad028
  Direction = (0,0,-1)
  Length = 0.5
  Length2 = 10
  Profile = -> Sketch049
  ReferenceAxis = -> Sketch049 [N_Axis]
  Refine = true
  Type = 0
FEATURE [Sketcher::SketchObject] Sketch050
  FullyConstrained = true
  MapMode = 5
  Placement = pos=(0,0,-0.5) rot=(1,0,0;3.14159rad)
  Support = -> [Pad029]
  sketch-geometry (1):
    g0: Circle CenterX=0 CenterY=0 CenterZ=0 NormalX=0 NormalY=0 NormalZ=1 AngleXU=0 Radius=10
  constraints (2):
    c: Coincident(g0,g-1)
    c: Diameter(g0) = 20
FEATURE [PartDesign::Pad] Pad030
  BaseFeature = -> Pad029
  Direction = (0,0,-1)
  Length = 2
  Length2 = 10
  Profile = -> Sketch050
  ReferenceAxis = -> Sketch050 [N_Axis]
  Refine = true
  Type = 0
FEATURE [Sketcher::SketchObject] Sketch051
  FullyConstrained = true
  MapMode = 5
  Placement = pos=(0,0,8.5) rot=(0,0,1;0rad)
  Support = -> [Pad030]
  sketch-geometry (3):
    g0: ArcOfCircle CenterX=0 CenterY=0 CenterZ=0 NormalX=0 NormalY=0 NormalZ=1 AngleXU=0 Radius=2.475 StartAngle=0.651099 EndAngle=5.63209
    g1: LineSegment StartX=1.96866 StartY=0 StartZ=0 EndX=1.96866 EndY=1.5 EndZ=0
    g2: LineSegment StartX=1.96866 StartY=0 StartZ=0 EndX=1.96866 EndY=-1.5 EndZ=0
  constraints (9):
    c: Coincident(g0,g-1)
    c: Diameter(g0) = 4.95
    c: PointOnObject(g1,g-1)
    c: Vertical(g1)
    c: Vertical(g2)
    c: Coincident(g0,g1)
    c: Coincident(g0,g2)
    c: Coincident(g1,g2)
    c: DistanceY(g1,g1) = 1.5
FEATURE [PartDesign::Pocket] Pocket013
  BaseFeature = -> Pad030
  Direction = (0,0,-1)
  Length = 50
  Length2 = 5
  Profile = -> Sketch051
  ReferenceAxis = -> Sketch051 [N_Axis]
  Refine = true
  Type = 0
FEATURE [PartDesign::CoordinateSystem] gear20_LCS
  AttacherType = Attacher::AttachEngine3D
FEATURE [PartDesign::Body] Body005  label="gear20"
  Group = -> [TimingGear002,Sketch046,Sketch047,Pad027,Sketch048,Pad028,Sketch049,Pad029,Sketch050,Pad030,Sketch051,Pocket013,gear20_LCS]
  Origin = -> Origin005
  Placement = pos=(0,0,45) rot=(0,0,1;0rad)
  Tip = -> Pocket013
COMPONENT P7 — recipe-attached ("gear60_2", modeled in this document).
Construction recipe (the document's own serialized feature program — sketch geometry with constraints, then the solid features built on it; lengths are millimeters unless a unit is written):

FEATURE [PartDesign::FeaturePython] TimingGear003  # WARN: FeaturePython — macro-defined, semantics opaque (R4)
  AttacherType = Attacher::AttachEngine3D
  h = 0.75
  height = 6
  num_teeth = 60
  offset = 0.4
  pitch = 2
  r0 = 0.555
  r1 = 1
  rs = 0.15
  type = 0
  u = 0.254
  version = 1.3.0
FEATURE [Sketcher::SketchObject] Sketch016
  FullyConstrained = true
  MapMode = 5
  Placement = pos=(0,0,0) rot=(1,0,0;3.14159rad)
  sketch-geometry (1):
    g0: Circle CenterX=0 CenterY=0 CenterZ=0 NormalX=0 NormalY=0 NormalZ=1 AngleXU=0 Radius=17.5
  constraints (2):
    c: Coincident(g0,g-1)
    c: Diameter(g0) = 35
FEATURE [PartDesign::Pad] Pad007
  BaseFeature = -> TimingGear003
  Direction = (0,0,-1)
  Length = 0.5
  Length2 = 10
  Profile = -> Sketch016
  ReferenceAxis = -> Sketch016 [N_Axis]
  Refine = true
  Type = 0
FEATURE [Sketcher::SketchObject] Sketch017
  FullyConstrained = true
  MapMode = 5
  Placement = pos=(0,0,6) rot=(0,0,1;0rad)
  sketch-geometry (1):
    g0: Circle CenterX=0 CenterY=0 CenterZ=0 NormalX=0 NormalY=0 NormalZ=1 AngleXU=0 Radius=17.5
  constraints (2):
    c: Coincident(g0,g-1)
    c: Diameter(g0) = 35
FEATURE [PartDesign::Pad] Pad008
  BaseFeature = -> Pad007
  Direction = (0,0,1)
  Length = 0.5
  Length2 = 10
  Profile = -> Sketch017
  ReferenceAxis = -> Sketch017 [N_Axis]
  Refine = true
  Type = 0
FEATURE [Sketcher::SketchObject] Sketch018
  FullyConstrained = true
  MapMode = 5
  Placement = pos=(0,0,6.5) rot=(0,0,1;0rad)
  sketch-geometry (1):
    g0: Circle CenterX=0 CenterY=0 CenterZ=0 NormalX=0 NormalY=0 NormalZ=1 AngleXU=0 Radius=21
  constraints (2):
    c: Coincident(g0,g-1)
    c: Diameter(g0) = 42
FEATURE [PartDesign::Pad] Pad009
  BaseFeature = -> Pad008
  Direction = (0,0,1)
  Length = 2
  Length2 = 10
  Profile = -> Sketch018
  ReferenceAxis = -> Sketch018 [N_Axis]
  Refine = true
  Type = 0
FEATURE [PartDesign::Fillet] Fillet
  Base = -> Pad009 [Edge4,Edge6,Edge1087]
  BaseFeature = -> Pad009
  Radius = 0.2
  Refine = true
  SupportTransform = false
  UseAllEdges = false
FEATURE [Sketcher::SketchObject] Sketch029
  FullyConstrained = true
  MapMode = 5
  Placement = pos=(0,0,8.5) rot=(0,0,1;0rad)
  Support = -> [Fillet]
  sketch-geometry (7):
    g0: LineSegment StartX=10 StartY=-5.7735 StartZ=0 EndX=0 EndY=11.547 EndZ=0
    g1: LineSegment StartX=0 StartY=11.547 StartZ=0 EndX=-10 EndY=-5.7735 EndZ=0
    g2: LineSegment StartX=-10 StartY=-5.7735 StartZ=0 EndX=10 EndY=-5.7735 EndZ=0
    g3: Circle CenterX=0 CenterY=0 CenterZ=0 NormalX=0 NormalY=0 NormalZ=1 AngleXU=0 Radius=11.547
    g4: Circle CenterX=10 CenterY=-5.7735 CenterZ=0 NormalX=0 NormalY=0 NormalZ=1 AngleXU=0 Radius=2.8
    g5: Circle CenterX=0 CenterY=11.547 CenterZ=0 NormalX=0 NormalY=0 NormalZ=1 AngleXU=0 Radius=2.8
    g6: Circle CenterX=-10 CenterY=-5.7735 CenterZ=0 NormalX=0 NormalY=0 NormalZ=1 AngleXU=0 Radius=2.8
  constraints (17):
    c: Coincident(g0,g1)
    c: Coincident(g1,g2)
    c: Coincident(g2,g0)
    c: Equal(g0,g1)
    c: Equal(g0,g2)
    c: PointOnObject(g0,g3)
    c: PointOnObject(g1,g3)
    c: PointOnObject(g2,g3)
    c: Coincident(g3,g-1)
    c: PointOnObject(g0,g-2)
    c: DistanceX(g2,g2) = 20
    c: Coincident(g4,g0)
    c: Coincident(g5,g0)
    c: Coincident(g6,g1)
    c: Equal(g5,g6)
    c: Equal(g6,g4)
    c: Diameter(g5) = 5.6
FEATURE [Sketcher::SketchObject] Sketch055
  FullyConstrained = true
  MapMode = 5
  Placement = pos=(0,0,-0.5) rot=(1,0,0;3.14159rad)
  Support = -> [Fillet]
  sketch-geometry (1):
    g0: Circle CenterX=0 CenterY=0 CenterZ=0 NormalX=0 NormalY=0 NormalZ=1 AngleXU=0 Radius=2.55
  constraints (2):
    c: Coincident(g0,g-1)
    c: Diameter(g0) = 5.1
FEATURE [PartDesign::Pocket] Pocket015
  BaseFeature = -> Fillet
  Direction = (0,0,1)
  Length = 12
  Length2 = 5
  Profile = -> Sketch055
  ReferenceAxis = -> Sketch055 [N_Axis]
  Refine = true
  Type = 0
FEATURE [PartDesign::Hole] Hole002
  BaseFeature = -> Pocket015
  CustomThreadClearance = 0
  Depth = 25
  DepthType = 0
  Diameter = 2.52
  DrillForDepth = true
  DrillPoint = 1
  DrillPointAngle = 118
  HoleCutCountersinkAngle = 90
  HoleCutCustomValues = false
  HoleCutDepth = 0
  HoleCutDiameter = 6.1
  HoleCutType = 2
  ModelThread = true
  Profile = -> Sketch029
  Refine = true
  Tapered = false
  TaperedAngle = 90
  ThreadClass = 0
  ThreadDepth = 25
  ThreadDepthType = 0
  ThreadDirection = 0
  ThreadFit = 0
  ThreadSize = 9
  ThreadType = 1
  Threaded = true
  UseCustomThreadClearance = false
FEATURE [PartDesign::Body] Body006  label="gear60_2"
  Group = -> [TimingGear003,Sketch016,Pad007,Sketch017,Pad008,Sketch018,Pad009,Fillet,Sketch029,Sketch055,Pocket015,Hole002]
  Origin = -> Origin006
  Placement = pos=(-45,3,56.75) rot=(0,0,1;0rad)
  Tip = -> Hole002
COMPONENT P8 — recipe-attached ("rod", modeled in this document).
Construction recipe (the document's own serialized feature program — sketch geometry with constraints, then the solid features built on it; lengths are millimeters unless a unit is written):

FEATURE [Sketcher::SketchObject] Sketch019
  FullyConstrained = true
  MapMode = 5
  sketch-geometry (1):
    g0: Circle CenterX=0 CenterY=0 CenterZ=0 NormalX=0 NormalY=0 NormalZ=1 AngleXU=0 Radius=6
  constraints (2):
    c: Coincident(g0,g-1)
    c: Diameter(g0) = 12
FEATURE [PartDesign::Pad] Pad010
  Direction = (0,0,1)
  Length = 400
  Length2 = 10
  Profile = -> Sketch019
  ReferenceAxis = -> Sketch019 [N_Axis]
  Refine = true
  Reversed = true
  Type = 0
FEATURE [Sketcher::SketchObject] Sketch071
  FullyConstrained = true
  MapMode = 5
  Support = -> [Pad010]
  sketch-geometry (1):
    g0: Circle CenterX=0 CenterY=0 CenterZ=0 NormalX=0 NormalY=0 NormalZ=1 AngleXU=0 Radius=12.5
  constraints (2):
    c: Coincident(g0,g-1)
    c: Diameter(g0) = 25
FEATURE [PartDesign::Body] Body007  label="rod"
  Group = -> [Sketch019,Pad010,Sketch071]
  Origin = -> Origin007
  Placement = pos=(3,54.9,405.8) rot=(0,0,1;0rad)
  Tip = -> Pad010
COMPONENT P9 — recipe-attached ("clamp", modeled in this document).
Construction recipe (the document's own serialized feature program — sketch geometry with constraints, then the solid features built on it; lengths are millimeters unless a unit is written):

FEATURE [Sketcher::SketchObject] Sketch025
  FullyConstrained = true
  MapMode = 5
  sketch-geometry (8):
    g0: ArcOfCircle CenterX=0 CenterY=0 CenterZ=0 NormalX=0 NormalY=0 NormalZ=1 AngleXU=0 Radius=8 StartAngle=3.466 EndAngle=9.29315
    g1: LineSegment StartX=-10.8095 StartY=2.2e-15 StartZ=0 EndX=-10.8095 EndY=1.05 EndZ=0
    g2: LineSegment StartX=-10.8095 StartY=1.05 StartZ=0 EndX=-7.93079 EndY=1.05 EndZ=0
    g3: LineSegment StartX=-10.8095 StartY=-1.5 StartZ=0 EndX=-10.8095 EndY=-2.55 EndZ=0
    g4: LineSegment StartX=-10.8095 StartY=-2.55 StartZ=0 EndX=-7.58271 EndY=-2.55 EndZ=0
    g5: ArcOfCircle CenterX=0 CenterY=0 CenterZ=0 NormalX=0 NormalY=0 NormalZ=1 AngleXU=0 Radius=6 StartAngle=3.39427 EndAngle=9.42478
    g6: LineSegment StartX=-10.8095 StartY=-1.5 StartZ=0 EndX=-5.80948 EndY=-1.5 EndZ=0
    g7: LineSegment StartX=-10.8095 StartY=2.2e-15 StartZ=0 EndX=-6 EndY=2.2e-15 EndZ=0
  constraints (23):
    c: Diameter(g0) = 16
    c: Vertical(g1)
    c: Coincident(g1,g2)
    c: Horizontal(g2)
    c: DistanceY(g1,g1) = 1.05
    c: Coincident(g0,g-1)
    c: Vertical(g3)
    c: Coincident(g3,g4)
    c: Horizontal(g4)
    c: Equal(g1,g3)
    c: Vertical(g3,g1)
    c: Coincident(g0,g5)
    c: Coincident(g0,g4)
    c: Coincident(g0,g2)
    c: Diameter(g5) = 12
    c: Coincident(g6,g3)
    c: Coincident(g6,g5)
    c: Horizontal(g6)
    c: Coincident(g7,g1)
    c: Coincident(g7,g5)
    c: DistanceX(g6,g6) = 5
    c: DistanceY(g5,g5) = 1.5
    c: Tangent(g7,g-1)
FEATURE [PartDesign::Pad] Pad013
  Direction = (0,0,1)
  Length = 10
  Length2 = 10
  Profile = -> Sketch025
  ReferenceAxis = -> Sketch025 [N_Axis]
  Refine = true
  Type = 0
FEATURE [PartDesign::Body] Body008  label="clamp"
  Group = -> [Sketch025,Pad013]
  Origin = -> Origin008
  Tip = -> Pad013
COMPONENT P10 — recipe-attached ("shaft", modeled in this document).
Construction recipe (the document's own serialized feature program — sketch geometry with constraints, then the solid features built on it; lengths are millimeters unless a unit is written):

FEATURE [Sketcher::SketchObject] Sketch039
  FullyConstrained = true
  MapMode = 5
  Support = -> [XY_Plane013]
  sketch-geometry (1):
    g0: Circle CenterX=0 CenterY=0 CenterZ=0 NormalX=0 NormalY=0 NormalZ=1 AngleXU=0 Radius=2.5
  constraints (2):
    c: Coincident(g0,g-1)
    c: Diameter(g0) = 5
FEATURE [PartDesign::Pad] Pad023
  Direction = (0,0,1)
  Length = 58
  Length2 = 10
  Profile = -> Sketch039
  ReferenceAxis = -> Sketch039 [N_Axis]
  Type = 0
FEATURE [Sketcher::SketchObject] Sketch040
  FullyConstrained = true
  MapMode = 5
  Placement = pos=(0,0,58) rot=(0,0,1;0rad)
  Support = -> [Pad023]
  sketch-geometry (2):
    g0: ArcOfCircle CenterX=0 CenterY=0 CenterZ=0 NormalX=0 NormalY=0 NormalZ=1 AngleXU=0 Radius=2.5 StartAngle=5.63968 EndAngle=6.92669
    g1: LineSegment StartX=2 StartY=1.5 StartZ=0 EndX=2 EndY=-1.5 EndZ=0
  constraints (6):
    c: Coincident(g0,g-1)
    c: Coincident(g1,g0)
    c: Coincident(g1,g0)
    c: Vertical(g1)
    c: Diameter(g0) = 5
    c: DistanceX(g0,g0) = 2
FEATURE [PartDesign::Pocket] Pocket003
  BaseFeature = -> Pad023
  Direction = (0,0,-1)
  Length = 18
  Length2 = 5
  Profile = -> Sketch040
  ReferenceAxis = -> Sketch040 [N_Axis]
  Type = 0
FEATURE [PartDesign::Chamfer] Chamfer002
  Angle = 45
  Base = -> Pocket003 [Edge5,Edge1]
  BaseFeature = -> Pocket003
  ChamferType = 1
  FlipDirection = false
  Size = 0.8
  Size2 = 0.4
  SupportTransform = false
  UseAllEdges = false
FEATURE [PartDesign::CoordinateSystem] shaft_LCS  label="shaftStepper_LCS"
  AttacherType = Attacher::AttachEngine3D
  Placement = pos=(0,0,30) rot=(0,0,1;0rad)
FEATURE [PartDesign::CoordinateSystem] rotating_LCS
  AttacherType = Attacher::AttachEngine3D
  Support = -> [Chamfer002]
FEATURE [PartDesign::Body] Body012  label="shaft"
  Group = -> [Sketch039,Pad023,Sketch040,Pocket003,Chamfer002,shaft_LCS,rotating_LCS]
  Origin = -> Origin013
  Placement = pos=(0,0,2.8) rot=(0,0,1;0rad)
  Tip = -> Chamfer002
COMPONENT P11 — recipe-attached ("AxleRod", modeled in this document).
Construction recipe (the document's own serialized feature program — sketch geometry with constraints, then the solid features built on it; lengths are millimeters unless a unit is written):

FEATURE [Sketcher::SketchObject] Sketch056
  FullyConstrained = true
  MapMode = 5
  Support = -> [XY_Plane017]
  sketch-geometry (12):
    g0: LineSegment StartX=-2.36 StartY=0.915 StartZ=0 EndX=-0.91 EndY=0.915 EndZ=0
    g1: LineSegment StartX=2.36 StartY=0.915 StartZ=0 EndX=2.36 EndY=-0.915 EndZ=0
    g2: LineSegment StartX=2.36 StartY=-0.915 StartZ=0 EndX=0.91 EndY=-0.915 EndZ=0
    g3: LineSegment StartX=-2.36 StartY=-0.915 StartZ=0 EndX=-2.36 EndY=0.915 EndZ=0
    g4: LineSegment StartX=0.91 StartY=-0.915 StartZ=0 EndX=0.91 EndY=-2.36 EndZ=0
    g5: LineSegment StartX=0.91 StartY=-2.36 StartZ=0 EndX=-0.91 EndY=-2.36 EndZ=0
    g6: LineSegment StartX=-0.91 StartY=-2.36 StartZ=0 EndX=-0.91 EndY=-0.915 EndZ=0
    g7: LineSegment StartX=-0.91 StartY=2.36 StartZ=0 EndX=-0.91 EndY=0.915 EndZ=0
    g8: LineSegment StartX=0.91 StartY=2.36 StartZ=0 EndX=-0.91 EndY=2.36 EndZ=0
    g9: LineSegment StartX=0.91 StartY=0.915 StartZ=0 EndX=0.91 EndY=2.36 EndZ=0
    g10: LineSegment StartX=0.91 StartY=0.915 StartZ=0 EndX=2.36 EndY=0.915 EndZ=0
    g11: LineSegment StartX=-0.91 StartY=-0.915 StartZ=0 EndX=-2.36 EndY=-0.915 EndZ=0
  constraints (32):
    c: Coincident(g10,g1)
    c: Coincident(g1,g2)
    c: Coincident(g11,g3)
    c: Coincident(g3,g0)
    c: Horizontal(g2)
    c: Vertical(g3)
    c: Symmetric(g10,g0,g-2)
    c: Symmetric(g1,g10,g-1)
    c: DistanceY(g1,g1) = 1.83
    c: DistanceX(g11,g2) = 4.72
    c: Vertical(g4)
    c: Coincident(g4,g5)
    c: Coincident(g5,g6)
    c: Vertical(g6)
    c: Symmetric(g5,g4,g-2)
    c: DistanceX(g5,g5) = 1.82
    c: Vertical(g9)
    c: Coincident(g9,g8)
    c: Coincident(g8,g7)
    c: Vertical(g7)
    c: Equal(g5,g8) = 1.82
    c: Symmetric(g7,g8,g-2)
    c: Equal(g9,g4)
    c: DistanceY(g9,g9) = 1.445
    c: Coincident(g0,g7)
    c: Coincident(g10,g9)
    c: Coincident(g2,g4)
    c: Coincident(g11,g6)
    c: Equal(g11,g2)
    c: Equal(g1,g3)
    c: Equal(g0,g10)
    c: Horizontal(g10)
FEATURE [PartDesign::Pad] Pad033
  Direction = (0,0,1)
  Length = 55
  Length2 = 10
  Profile = -> Sketch056
  ReferenceAxis = -> Sketch056 [N_Axis]
  Refine = true
  Type = 0
FEATURE [PartDesign::Body] Body016  label="AxleRod"
  Group = -> [Sketch056,Pad033]
  Origin = -> Origin017
  Placement = pos=(8,-13,-145) rot=(0,0,1;0rad)
  Tip = -> Pad033
COMPONENT P12 — recipe-attached ("semi_stationaryTop001", modeled in this document).
Construction recipe (the document's own serialized feature program — sketch geometry with constraints, then the solid features built on it; lengths are millimeters unless a unit is written):

FEATURE [Sketcher::SketchObject] Sketch086
  FullyConstrained = true
  MapMode = 5
  sketch-geometry (7):
    g0: LineSegment StartX=86.6025 StartY=50 StartZ=0 EndX=-1.42e-14 EndY=100 EndZ=0
    g1: LineSegment StartX=-1.42e-14 StartY=100 StartZ=0 EndX=-86.6025 EndY=50 EndZ=0
    g2: LineSegment StartX=-86.6025 StartY=50 StartZ=0 EndX=-86.6025 EndY=-50 EndZ=0
    g3: LineSegment StartX=-86.6025 StartY=-50 StartZ=0 EndX=0 EndY=-100 EndZ=0
    g4: LineSegment StartX=0 StartY=-100 StartZ=0 EndX=86.6025 EndY=-50 EndZ=0
    g5: LineSegment StartX=86.6025 StartY=-50 StartZ=0 EndX=86.6025 EndY=50 EndZ=0
    g6: Circle CenterX=0 CenterY=0 CenterZ=0 NormalX=0 NormalY=0 NormalZ=1 AngleXU=0 Radius=100
  constraints (16):
    c: Coincident(g0,g1)
    c: Coincident(g1,g2)
    c: Coincident(g2,g3)
    c: Coincident(g3,g4)
    c: Coincident(g4,g5)
    c: Coincident(g5,g0)
    c: Equal(g0, g1-g5) x5
    c: PointOnObject(g0,g6)
    c: PointOnObject(g1,g6)
    c: PointOnObject(g2,g6)
    c: PointOnObject(g3,g6)
    c: PointOnObject(g4,g6)
    c: PointOnObject(g5,g6)
    c: Coincident(g6,g-1)
    c: PointOnObject(g3,g-2)
    c: DistanceY(g5,g5) = 100
FEATURE [PartDesign::Pad] Pad041
  Direction = (0,0,1)
  Length = 10
  Length2 = 10
  Profile = -> Sketch086
  ReferenceAxis = -> Sketch086 [N_Axis]
  Refine = true
  Type = 0
FEATURE [Sketcher::SketchObject] Sketch087  label="lock002"
  FullyConstrained = true
  MapMode = 5
  Placement = pos=(0,0,10) rot=(0,0,1;0rad)
  sketch-geometry (1):
    g0: Circle CenterX=0 CenterY=0 CenterZ=0 NormalX=0 NormalY=0 NormalZ=1 AngleXU=0 Radius=15
  constraints (2):
    c: Coincident(g0,g-1)
    c: Diameter(g0) = 30
FEATURE [Sketcher::SketchObject] Sketch088  label="press_fit001"
  FullyConstrained = true
  MapMode = 5
  Placement = pos=(0,0,0) rot=(1,0,0;3.14159rad)
  sketch-geometry (1):
    g0: Circle CenterX=0 CenterY=0 CenterZ=0 NormalX=0 NormalY=0 NormalZ=1 AngleXU=0 Radius=15.975
  constraints (2):
    c: Coincident(g0,g-1)
    c: Diameter(g0) = 31.95
FEATURE [PartDesign::Pocket] Pocket017
  BaseFeature = -> Pad041
  Direction = (0,1e-16,1)
  Length = 5
  Length2 = 5
  Profile = -> Sketch088
  ReferenceAxis = -> Sketch088 [N_Axis]
  Refine = true
  Type = 0
FEATURE [PartDesign::Pocket] Pocket018
  BaseFeature = -> Pocket017
  Direction = (0,0,-1)
  Length = 5
  Length2 = 5
  Profile = -> Sketch087
  ReferenceAxis = -> Sketch087 [N_Axis]
  Refine = true
  Type = 0
FEATURE [Sketcher::SketchObject] Sketch089
  FullyConstrained = true
  MapMode = 5
  Placement = pos=(0,0,10) rot=(0,0,1;0rad)
  Support = -> [Pocket018]
  sketch-geometry (7):
    g0: LineSegment StartX=35 StartY=-20.2073 StartZ=0 EndX=0 EndY=40.4145 EndZ=0
    g1: LineSegment StartX=0 StartY=40.4145 StartZ=0 EndX=-35 EndY=-20.2073 EndZ=0
    g2: LineSegment StartX=-35 StartY=-20.2073 StartZ=0 EndX=35 EndY=-20.2073 EndZ=0
    g3: Circle CenterX=0 CenterY=0 CenterZ=0 NormalX=0 NormalY=0 NormalZ=1 AngleXU=0 Radius=40.4145
    g4: Circle CenterX=0 CenterY=40.4145 CenterZ=0 NormalX=0 NormalY=0 NormalZ=1 AngleXU=0 Radius=3
    g5: Circle CenterX=35 CenterY=-20.2073 CenterZ=0 NormalX=0 NormalY=0 NormalZ=1 AngleXU=0 Radius=3
    g6: Circle CenterX=-35 CenterY=-20.2073 CenterZ=0 NormalX=0 NormalY=0 NormalZ=1 AngleXU=0 Radius=3
  constraints (17):
    c: Coincident(g0,g1)
    c: Coincident(g1,g2)
    c: Coincident(g2,g0)
    c: Equal(g0,g1)
    c: Equal(g0,g2)
    c: PointOnObject(g0,g3)
    c: PointOnObject(g1,g3)
    c: PointOnObject(g2,g3)
    c: Coincident(g3,g-1)
    c: PointOnObject(g0,g-2)
    c: DistanceX(g2,g2) = 70
    c: Coincident(g4,g0)
    c: Coincident(g5,g0)
    c: Coincident(g6,g1)
    c: Equal(g4,g6)
    c: Equal(g6,g5)
    c: Diameter(g4) = 6
FEATURE [PartDesign::Hole] Hole016
  BaseFeature = -> Pocket018
  CustomThreadClearance = 0
  Depth = 25
  DepthType = 0
  Diameter = 2.52
  DrillForDepth = false
  DrillPoint = 1
  DrillPointAngle = 118
  HoleCutCountersinkAngle = 90
  HoleCutCustomValues = false
  HoleCutDepth = 0
  HoleCutDiameter = 6.1
  HoleCutType = 2
  ModelThread = true
  Profile = -> Sketch089
  Refine = true
  Tapered = false
  TaperedAngle = 90
  ThreadClass = 0
  ThreadDepth = 25
  ThreadDepthType = 0
  ThreadDirection = 0
  ThreadFit = 0
  ThreadSize = 9
  ThreadType = 1
  Threaded = true
  UseCustomThreadClearance = false
FEATURE [Sketcher::SketchObject] Sketch090
  FullyConstrained = true
  MapMode = 5
  Placement = pos=(86.6025,-5.664e-13,0) rot=(0.57735,0.57735,0.57735;2.0944rad)
  Support = -> [Hole016]
  sketch-geometry (1):
    g0: Circle CenterX=0 CenterY=5 CenterZ=0 NormalX=0 NormalY=0 NormalZ=1 AngleXU=0 Radius=3
  constraints (3):
    c: PointOnObject(g0,g-2)
    c: Diameter(g0) = 6
    c: DistanceY(g-1,g0) = 5
FEATURE [PartDesign::Hole] Hole017
  BaseFeature = -> Hole016
  CustomThreadClearance = 0
  Depth = 15
  DepthType = 0
  Diameter = 2.52
  DrillForDepth = true
  DrillPoint = 1
  DrillPointAngle = 118
  HoleCutCountersinkAngle = 90
  HoleCutCustomValues = false
  HoleCutDepth = 0
  HoleCutDiameter = 6.1
  HoleCutType = 0
  ModelThread = true
  Profile = -> Sketch090
  Refine = true
  Tapered = false
  TaperedAngle = 90
  ThreadClass = 0
  ThreadDepth = 15
  ThreadDepthType = 0
  ThreadDirection = 0
  ThreadFit = 0
  ThreadSize = 9
  ThreadType = 1
  Threaded = true
  UseCustomThreadClearance = false
FEATURE [Sketcher::SketchObject] Sketch091
  FullyConstrained = true
  MapMode = 5
  Placement = pos=(-43.3013,75,0) rot=(-0.186157,0.694747,0.694747;3.50969rad)
  Support = -> [Hole017]
  sketch-geometry (1):
    g0: Circle CenterX=0 CenterY=5 CenterZ=0 NormalX=0 NormalY=0 NormalZ=1 AngleXU=0 Radius=3
  constraints (3):
    c: PointOnObject(g0,g-2)
    c: Diameter(g0) = 6
    c: DistanceY(g-1,g0) = 5
FEATURE [PartDesign::Hole] Hole018
  BaseFeature = -> Hole017
  CustomThreadClearance = 0
  Depth = 15
  DepthType = 0
  Diameter = 2.52
  DrillForDepth = true
  DrillPoint = 1
  DrillPointAngle = 118
  HoleCutCountersinkAngle = 90
  HoleCutCustomValues = false
  HoleCutDepth = 0
  HoleCutDiameter = 6.1
  HoleCutType = 0
  ModelThread = true
  Profile = -> Sketch091
  Refine = true
  Tapered = false
  TaperedAngle = 90
  ThreadClass = 0
  ThreadDepth = 15
  ThreadDepthType = 0
  ThreadDirection = 0
  ThreadFit = 0
  ThreadSize = 9
  ThreadType = 1
  Threaded = true
  UseCustomThreadClearance = false
FEATURE [Sketcher::SketchObject] Sketch092
  FullyConstrained = true
  MapMode = 5
  Placement = pos=(-43.3013,-75,0) rot=(0.935113,-0.250563,-0.250563;1.63783rad)
  Support = -> [Hole018]
  sketch-geometry (1):
    g0: Circle CenterX=0 CenterY=5 CenterZ=0 NormalX=0 NormalY=0 NormalZ=1 AngleXU=0 Radius=3
  constraints (3):
    c: PointOnObject(g0,g-2)
    c: Diameter(g0) = 6
    c: DistanceY(g-1,g0) = 5
FEATURE [PartDesign::Hole] Hole019
  BaseFeature = -> Hole018
  CustomThreadClearance = 0
  Depth = 15
  DepthType = 0
  Diameter = 2.52
  DrillForDepth = true
  DrillPoint = 1
  DrillPointAngle = 118
  HoleCutCountersinkAngle = 90
  HoleCutCustomValues = false
  HoleCutDepth = 0
  HoleCutDiameter = 6.1
  HoleCutType = 0
  ModelThread = true
  Profile = -> Sketch092
  Refine = true
  Tapered = false
  TaperedAngle = 90
  ThreadClass = 0
  ThreadDepth = 15
  ThreadDepthType = 0
  ThreadDirection = 0
  ThreadFit = 0
  ThreadSize = 9
  ThreadType = 1
  Threaded = true
  UseCustomThreadClearance = false
FEATURE [PartDesign::Body] Body019  label="semi_stationaryTop001"
  Group = -> [Sketch086,Pad041,Sketch087,Sketch088,Pocket017,Pocket018,Sketch089,Hole016,Sketch090,Hole017,Sketch091,Hole018,Sketch092,Hole019]
  Origin = -> Origin027
  Placement = pos=(3.15,54.87,273.3) rot=(0,0,1;0rad)
  Tip = -> Hole019
COMPONENT P13 — recipe-attached ("semi_stationarybottom001", modeled in this document).
Construction recipe (the document's own serialized feature program — sketch geometry with constraints, then the solid features built on it; lengths are millimeters unless a unit is written):

FEATURE [Sketcher::SketchObject] Sketch093
  FullyConstrained = true
  MapMode = 5
  sketch-geometry (7):
    g0: LineSegment StartX=86.6025 StartY=50 StartZ=0 EndX=-1.42e-14 EndY=100 EndZ=0
    g1: LineSegment StartX=-1.42e-14 StartY=100 StartZ=0 EndX=-86.6025 EndY=50 EndZ=0
    g2: LineSegment StartX=-86.6025 StartY=50 StartZ=0 EndX=-86.6025 EndY=-50 EndZ=0
    g3: LineSegment StartX=-86.6025 StartY=-50 StartZ=0 EndX=0 EndY=-100 EndZ=0
    g4: LineSegment StartX=0 StartY=-100 StartZ=0 EndX=86.6025 EndY=-50 EndZ=0
    g5: LineSegment StartX=86.6025 StartY=-50 StartZ=0 EndX=86.6025 EndY=50 EndZ=0
    g6: Circle CenterX=0 CenterY=0 CenterZ=0 NormalX=0 NormalY=0 NormalZ=1 AngleXU=0 Radius=100
  constraints (16):
    c: Coincident(g0,g1)
    c: Coincident(g1,g2)
    c: Coincident(g2,g3)
    c: Coincident(g3,g4)
    c: Coincident(g4,g5)
    c: Coincident(g5,g0)
    c: Equal(g0, g1-g5) x5
    c: PointOnObject(g0,g6)
    c: PointOnObject(g1,g6)
    c: PointOnObject(g2,g6)
    c: PointOnObject(g3,g6)
    c: PointOnObject(g4,g6)
    c: PointOnObject(g5,g6)
    c: Coincident(g6,g-1)
    c: PointOnObject(g3,g-2)
    c: DistanceY(g5,g5) = 100
FEATURE [PartDesign::Pad] Pad042
  Direction = (0,0,1)
  Length = 10
  Length2 = 10
  Profile = -> Sketch093
  ReferenceAxis = -> Sketch093 [N_Axis]
  Refine = true
  Type = 0
FEATURE [Sketcher::SketchObject] Sketch094  label="lock003"
  FullyConstrained = true
  MapMode = 5
  Placement = pos=(0,0,10) rot=(0,0,1;0rad)
  sketch-geometry (1):
    g0: Circle CenterX=0 CenterY=0 CenterZ=0 NormalX=0 NormalY=0 NormalZ=1 AngleXU=0 Radius=15
  constraints (2):
    c: Coincident(g0,g-1)
    c: Diameter(g0) = 30
FEATURE [Sketcher::SketchObject] Sketch095  label="press-fit001"
  FullyConstrained = true
  MapMode = 5
  Placement = pos=(0,0,0) rot=(1,0,0;3.14159rad)
  sketch-geometry (1):
    g0: Circle CenterX=0 CenterY=0 CenterZ=0 NormalX=0 NormalY=0 NormalZ=1 AngleXU=0 Radius=15.975
  constraints (2):
    c: Coincident(g0,g-1)
    c: Diameter(g0) = 31.95
FEATURE [PartDesign::Pocket] Pocket019
  BaseFeature = -> Pad042
  Direction = (0,0,1)
  Length = 5
  Length2 = 5
  Profile = -> Sketch095
  ReferenceAxis = -> Sketch095 [N_Axis]
  Refine = true
  Type = 0
FEATURE [PartDesign::Pocket] Pocket020
  BaseFeature = -> Pocket019
  Direction = (0,0,-1)
  Length = 5
  Length2 = 5
  Profile = -> Sketch094
  ReferenceAxis = -> Sketch094 [N_Axis]
  Refine = true
  Type = 0
FEATURE [Sketcher::SketchObject] Sketch096
  FullyConstrained = true
  MapMode = 5
  Placement = pos=(0,0,10) rot=(0,0,1;0rad)
  sketch-geometry (7):
    g0: LineSegment StartX=35 StartY=-20.2073 StartZ=0 EndX=0 EndY=40.4145 EndZ=0
    g1: LineSegment StartX=0 StartY=40.4145 StartZ=0 EndX=-35 EndY=-20.2073 EndZ=0
    g2: LineSegment StartX=-35 StartY=-20.2073 StartZ=0 EndX=35 EndY=-20.2073 EndZ=0
    g3: Circle CenterX=0 CenterY=0 CenterZ=0 NormalX=0 NormalY=0 NormalZ=1 AngleXU=0 Radius=40.4145
    g4: Circle CenterX=35 CenterY=-20.2073 CenterZ=0 NormalX=0 NormalY=0 NormalZ=1 AngleXU=0 Radius=3
    g5: Circle CenterX=0 CenterY=40.4145 CenterZ=0 NormalX=0 NormalY=0 NormalZ=1 AngleXU=0 Radius=3
    g6: Circle CenterX=-35 CenterY=-20.2073 CenterZ=0 NormalX=0 NormalY=0 NormalZ=1 AngleXU=0 Radius=3
  constraints (17):
    c: Coincident(g0,g1)
    c: Coincident(g1,g2)
    c: Coincident(g2,g0)
    c: Equal(g0,g1)
    c: Equal(g0,g2)
    c: PointOnObject(g0,g3)
    c: PointOnObject(g1,g3)
    c: PointOnObject(g2,g3)
    c: Coincident(g3,g-1)
    c: PointOnObject(g0,g-2)
    c: DistanceX(g2,g2) = 70
    c: Coincident(g4,g0)
    c: Diameter(g4) = 6
    c: Coincident(g5,g0)
    c: Coincident(g6,g1)
    c: Equal(g6,g5)
    c: Equal(g5,g4)
FEATURE [PartDesign::Hole] Hole020
  BaseFeature = -> Pocket020
  CustomThreadClearance = 0
  Depth = 7
  DepthType = 0
  Diameter = 2.52
  DrillForDepth = true
  DrillPoint = 1
  DrillPointAngle = 118
  HoleCutCountersinkAngle = 90
  HoleCutCustomValues = false
  HoleCutDepth = 0
  HoleCutDiameter = 6.1
  HoleCutType = 0
  ModelThread = true
  Profile = -> Sketch096
  Refine = true
  Tapered = false
  TaperedAngle = 90
  ThreadClass = 0
  ThreadDepth = 7
  ThreadDepthType = 0
  ThreadDirection = 0
  ThreadFit = 0
  ThreadSize = 9
  ThreadType = 1
  Threaded = true
  UseCustomThreadClearance = false
FEATURE [Sketcher::SketchObject] Sketch097
  FullyConstrained = true
  MapMode = 5
  Placement = pos=(0,0,0) rot=(1,0,0;3.14159rad)
  Support = -> [Hole020]
  sketch-geometry (7):
    g0: LineSegment StartX=35 StartY=-20.2073 StartZ=0 EndX=0 EndY=40.4145 EndZ=0
    g1: LineSegment StartX=0 StartY=40.4145 StartZ=0 EndX=-35 EndY=-20.2073 EndZ=0
    g2: LineSegment StartX=-35 StartY=-20.2073 StartZ=0 EndX=35 EndY=-20.2073 EndZ=0
    g3: Circle CenterX=0 CenterY=0 CenterZ=0 NormalX=0 NormalY=0 NormalZ=1 AngleXU=0 Radius=40.4145
    g4: Circle CenterX=35 CenterY=-20.2073 CenterZ=0 NormalX=0 NormalY=0 NormalZ=1 AngleXU=0 Radius=3
    g5: Circle CenterX=0 CenterY=40.4145 CenterZ=0 NormalX=0 NormalY=0 NormalZ=1 AngleXU=0 Radius=3
    g6: Circle CenterX=-35 CenterY=-20.2073 CenterZ=0 NormalX=0 NormalY=0 NormalZ=1 AngleXU=0 Radius=3
  constraints (17):
    c: Coincident(g0,g1)
    c: Coincident(g1,g2)
    c: Coincident(g2,g0)
    c: Equal(g0,g1)
    c: Equal(g0,g2)
    c: PointOnObject(g0,g3)
    c: PointOnObject(g1,g3)
    c: PointOnObject(g2,g3)
    c: Coincident(g3,g-1)
    c: PointOnObject(g0,g-2)
    c: DistanceX(g2,g2) = 70
    c: Coincident(g4,g0)
    c: Coincident(g5,g0)
    c: Coincident(g6,g1)
    c: Equal(g6,g4)
    c: Equal(g4,g5)
    c: Diameter(g5) = 6
FEATURE [PartDesign::Hole] Hole021
  BaseFeature = -> Hole020
  CustomThreadClearance = 0
  Depth = 7
  DepthType = 0
  Diameter = 2.52
  DrillForDepth = true
  DrillPoint = 1
  DrillPointAngle = 118
  HoleCutCountersinkAngle = 90
  HoleCutCustomValues = false
  HoleCutDepth = 0
  HoleCutDiameter = 6.1
  HoleCutType = 0
  ModelThread = true
  Profile = -> Sketch097
  Refine = true
  Tapered = false
  TaperedAngle = 90
  ThreadClass = 0
  ThreadDepth = 7
  ThreadDepthType = 0
  ThreadDirection = 0
  ThreadFit = 0
  ThreadSize = 9
  ThreadType = 1
  Threaded = true
  UseCustomThreadClearance = false
FEATURE [PartDesign::Body] Body020  label="semi_stationarybottom001"
  Group = -> [Sketch093,Pad042,Sketch094,Sketch095,Pocket019,Pocket020,Sketch096,Hole020,Sketch097,Hole021]
  Origin = -> Origin028
  Placement = pos=(3.1,54.8,273.3) rot=(1,0,0;3.14159rad)
  Tip = -> Hole021
COMPONENT P14 — recipe-attached ("17HS4401S Stepper Motor", modeled in this document).
Construction recipe (the document's own serialized feature program — sketch geometry with constraints, then the solid features built on it; lengths are millimeters unless a unit is written):

FEATURE [Sketcher::SketchObject] Sketch031  label=" rear outline"
  FullyConstrained = true
  MapMode = 5
  Support = -> [XY_Plane009]
  sketch-geometry (17):
    g0: ArcOfCircle CenterX=0 CenterY=0 CenterZ=0 NormalX=0 NormalY=0 NormalZ=1 AngleXU=0 Radius=26.8 StartAngle=2.24118 EndAngle=2.47121
    g1: ArcOfCircle CenterX=0 CenterY=0 CenterZ=0 NormalX=0 NormalY=0 NormalZ=1 AngleXU=0 Radius=26.8 StartAngle=5.38277 EndAngle=5.6128
    g2: ArcOfCircle CenterX=0 CenterY=0 CenterZ=0 NormalX=0 NormalY=0 NormalZ=1 AngleXU=0 Radius=26.8 StartAngle=0.670386 EndAngle=0.900411
    g3: ArcOfCircle CenterX=0 CenterY=0 CenterZ=0 NormalX=0 NormalY=0 NormalZ=1 AngleXU=0 Radius=26.8 StartAngle=3.81198 EndAngle=4.042
    g4: LineSegment StartX=-16.6505 StartY=21 StartZ=0 EndX=16.6505 EndY=21 EndZ=0
    g5: LineSegment StartX=21 StartY=16.6505 StartZ=0 EndX=21 EndY=8.3 EndZ=0
    g6: LineSegment StartX=-16.6505 StartY=-21 StartZ=0 EndX=16.6505 EndY=-21 EndZ=0
    g7: LineSegment StartX=-21 StartY=16.6505 StartZ=0 EndX=-21 EndY=-16.6505 EndZ=0
    g8: Circle CenterX=0 CenterY=0 CenterZ=0 NormalX=0 NormalY=0 NormalZ=1 AngleXU=0 Radius=4.5
    g9: Circle CenterX=-15.5 CenterY=15.5 CenterZ=0 NormalX=0 NormalY=0 NormalZ=1 AngleXU=0 Radius=1.5
    g10: Circle CenterX=15.5 CenterY=15.5 CenterZ=0 NormalX=0 NormalY=0 NormalZ=1 AngleXU=0 Radius=1.5
    g11: Circle CenterX=15.5 CenterY=-15.5 CenterZ=0 NormalX=0 NormalY=0 NormalZ=1 AngleXU=0 Radius=1.5
    g12: Circle CenterX=-15.5 CenterY=-15.5 CenterZ=0 NormalX=0 NormalY=0 NormalZ=1 AngleXU=0 Radius=1.5
    g13: LineSegment StartX=21 StartY=8.3 StartZ=0 EndX=25.4 EndY=8.3 EndZ=0
    g14: LineSegment StartX=25.4 StartY=8.3 StartZ=0 EndX=25.4 EndY=-8.3 EndZ=0
    g15: LineSegment StartX=25.4 StartY=-8.3 StartZ=0 EndX=21 EndY=-8.3 EndZ=0
    g16: LineSegment StartX=21 StartY=-8.3 StartZ=0 EndX=21 EndY=-16.6505 EndZ=0
  constraints (50):
    c: Coincident(g0,g-1)
    c: Coincident(g1,g0)
    c: Coincident(g2,g0)
    c: Coincident(g3,g0)
    c: Equal(g0,g1)
    c: Equal(g1,g2)
    c: Equal(g2,g3)
    c: Radius(g0) = 26.8
    c: Coincident(g4,g0)
    c: Coincident(g4,g2)
    c: Horizontal(g4)
    c: Coincident(g5,g2)
    c: Coincident(g16,g1)
    c: Vertical(g5)
    c: Coincident(g6,g3)
    c: Coincident(g6,g1)
    c: Coincident(g7,g0)
    c: Coincident(g7,g3)
    c: Vertical(g7)
    c: Horizontal(g6)
    c: DistanceX(g0,g2) = 42
    c: DistanceY(g1,g2) = 42
    c: DistanceY(g0,g2) = 21
    c: DistanceX(g0,g0) = 21
    c: Coincident(g8,g0)
    c: Diameter(g8) = 9
    c: Vertical(g9,g12)
    c: Vertical(g11,g10)
    c: Horizontal(g9,g10)
    c: Horizontal(g12,g11)
    c: Equal(g9,g10)
    c: Equal(g11,g10)
    c: Equal(g11,g12)
    c: Diameter(g9) = 3
    c: DistanceX(g9,g10) = 31
    c: DistanceY(g11,g10) = 31
    c: DistanceY(g0,g10) = 15.5
    c: DistanceX(g0,g10) = 15.5
    c: Horizontal(g13)
    c: Coincident(g14,g13)
    c: Vertical(g14)
    c: Coincident(g15,g14)
    c: Horizontal(g15)
    c: DistanceY(g14,g14) = 16.6
    c: DistanceY(g0,g13) = 8.3
    c: DistanceX(g13,g13) = 4.4
    c: Coincident(g5,g13)
    c: Coincident(g16,g15)
    c: Vertical(g5,g15)
    c: Vertical(g16)
FEATURE [PartDesign::Pad] Pad017
  Direction = (0,0,1)
  Length = 9.4
  Length2 = 10
  Profile = -> Sketch031
  ReferenceAxis = -> Sketch031 [N_Axis]
  Type = 0
FEATURE [Sketcher::SketchObject] Sketch033
  FullyConstrained = true
  MapMode = 5
  Support = -> [XY_Plane009]
  sketch-geometry (4):
    g0: Circle CenterX=-15.5 CenterY=15.5 CenterZ=0 NormalX=0 NormalY=0 NormalZ=1 AngleXU=0 Radius=3.2
    g1: Circle CenterX=15.5 CenterY=15.5 CenterZ=0 NormalX=0 NormalY=0 NormalZ=1 AngleXU=0 Radius=3.2
    g2: Circle CenterX=15.5 CenterY=-15.5 CenterZ=0 NormalX=0 NormalY=0 NormalZ=1 AngleXU=0 Radius=3.2
    g3: Circle CenterX=-15.5 CenterY=-15.5 CenterZ=0 NormalX=0 NormalY=0 NormalZ=1 AngleXU=0 Radius=3.2
  constraints (12):
    c: Equal(g0,g1)
    c: Equal(g1,g2)
    c: Equal(g2,g3)
    c: Horizontal(g0,g1)
    c: Horizontal(g3,g2)
    c: Vertical(g1,g2)
    c: Vertical(g0,g3)
    c: Diameter(g0) = 6.4
    c: DistanceY(g2,g1) = 31
    c: DistanceY(g2,g-1) = 15.5
    c: DistanceX(g0,g1) = 31
    c: DistanceX(g-1,g1) = 15.5
FEATURE [PartDesign::Pocket] Pocket011  label="screw counterbore"
  BaseFeature = -> Pad017
  Direction = (0,0,-1)
  Length = 3
  Length2 = 5
  Profile = -> Sketch033
  ReferenceAxis = -> Sketch033 [N_Axis]
  Reversed = true
  Type = 0
FEATURE [Sketcher::SketchObject] Sketch034
  AttachmentOffset = pos=(0,0,10) rot=(0,0,1;0rad)
  FullyConstrained = true
  MapMode = 5
  Placement = pos=(0,0,10) rot=(0,0,1;0rad)
  Support = -> [XY_Plane009]
  sketch-geometry (1):
    g0: Circle CenterX=0 CenterY=0 CenterZ=0 NormalX=0 NormalY=0 NormalZ=1 AngleXU=0 Radius=8
  constraints (2):
    c: Coincident(g0,g-1)
    c: Diameter(g0) = 16
FEATURE [PartDesign::Pocket] Pocket001  label="bearing pocket"
  BaseFeature = -> Pocket011
  Direction = (0,0,-1)
  Length = 8
  Length2 = 5
  Profile = -> Sketch034
  ReferenceAxis = -> Sketch034 [N_Axis]
  Type = 0
FEATURE [Sketcher::SketchObject] Sketch004
  AttachmentOffset = pos=(0,0,26) rot=(0,0,1;0rad)
  FullyConstrained = true
  MapMode = 5
  Placement = pos=(26,-5.8e-15,5.8e-15) rot=(0.57735,0.57735,0.57735;2.0944rad)
  Support = -> [YZ_Plane009]
  sketch-geometry (4):
    g0: LineSegment StartX=-8.3 StartY=9.4 StartZ=0 EndX=8.3 EndY=9.4 EndZ=0
    g1: LineSegment StartX=8.3 StartY=9.4 StartZ=0 EndX=8.3 EndY=3 EndZ=0
    g2: LineSegment StartX=8.3 StartY=3 StartZ=0 EndX=-8.3 EndY=3 EndZ=0
    g3: LineSegment StartX=-8.3 StartY=3 StartZ=0 EndX=-8.3 EndY=9.4 EndZ=0
  constraints (12):
    c: Coincident(g0,g1)
    c: Coincident(g1,g2)
    c: Coincident(g2,g3)
    c: Coincident(g3,g0)
    c: Horizontal(g0)
    c: Horizontal(g2)
    c: Vertical(g1)
    c: Vertical(g3)
    c: DistanceX(g0,g0) = 16.6
    c: DistanceX(g-1,g0) = 8.3
    c: DistanceY(g-1,g0) = 9.4
    c: DistanceY(g-1,g1) = 3
FEATURE [PartDesign::Pocket] Pocket012
  BaseFeature = -> Pocket001
  Direction = (-1,2e-16,-3e-16)
  Length = 10
  Length2 = 5
  Profile = -> Sketch004
  ReferenceAxis = -> Sketch004 [N_Axis]
  Type = 0
FEATURE [PartDesign::Fillet] Fillet002
  Base = -> Pocket012 [Edge48,Edge5,Edge40,Edge45,Edge52,Edge53,Edge50,Edge47,Edge44,Edge9,Edge2,Edge1,Edge24,Edge21,Edge22,Edge25]
  BaseFeature = -> Pocket012
  Radius = 0.4
  SupportTransform = false
  UseAllEdges = false
FEATURE [PartDesign::Fillet] Fillet003
  Base = -> Fillet002 [Edge27]
  BaseFeature = -> Fillet002
  Radius = 0.4
  SupportTransform = false
  UseAllEdges = false
FEATURE [PartDesign::Body] Body009  label="rear end cap"
  Group = -> [Sketch031,Pad017,Sketch033,Pocket011,Sketch034,Pocket001,Sketch004,Pocket012,Fillet002,Fillet003]
  Origin = -> Origin009
  Tip = -> Fillet003
FEATURE [Sketcher::SketchObject] Sketch035
  FullyConstrained = true
  MapMode = 5
  Placement = pos=(0,0,0) rot=(1,0,0;1.5708rad)
  Support = -> [XZ_Plane011]
  sketch-geometry (12):
    g0: LineSegment StartX=2.5 StartY=2.55 StartZ=0 EndX=8 EndY=2.55 EndZ=0
    g1: LineSegment StartX=8 StartY=2.55 StartZ=0 EndX=8 EndY=-2.45 EndZ=0
    g2: LineSegment StartX=8 StartY=-2.45 StartZ=0 EndX=6.5 EndY=-2.45 EndZ=0
    g3: LineSegment StartX=2.5 StartY=-2.5 StartZ=0 EndX=2.5 EndY=2.55 EndZ=0
    g4: LineSegment StartX=4.2 StartY=-2.45 StartZ=0 EndX=4.1 EndY=-1.95 EndZ=0
    g5: LineSegment StartX=4.1 StartY=-1.95 StartZ=0 EndX=4 EndY=-2.5 EndZ=0
    g6: LineSegment StartX=5.2 StartY=-2.45 StartZ=0 EndX=6.13734 EndY=-1.97682 EndZ=0
    g7: LineSegment StartX=6.5 StartY=-2.2 StartZ=0 EndX=6.5 EndY=-2.45 EndZ=0
    g8: LineSegment StartX=4 StartY=-2.5 StartZ=0 EndX=2.5 EndY=-2.5 EndZ=0
    g9: LineSegment StartX=5.2 StartY=-2.45 StartZ=0 EndX=4.2 EndY=-2.45 EndZ=0
    g10: ArcOfCircle CenterX=6.25 CenterY=-2.2 CenterZ=0 NormalX=0 NormalY=0 NormalZ=1 AngleXU=0 Radius=0.25 StartAngle=2.03828 EndAngle=6.28319
    g11: LineSegment StartX=6.5 StartY=-2.45 StartZ=0 EndX=5.2 EndY=-2.45 EndZ=0
  constraints (34):
    c: Coincident(g0,g1)
    c: Coincident(g1,g2)
    c: Coincident(g8,g3)
    c: Coincident(g3,g0)
    c: Horizontal(g0)
    c: Horizontal(g2)
    c: Vertical(g1)
    c: Vertical(g3)
    c: Coincident(g5,g4)
    c: DistanceX(g-1,g8) = 2.5
    c: DistanceX(g-1,g1) = 8
    c: DistanceY(g1,g1) = 5
    c: DistanceY(g8,g-1) = 2.5
    c: Coincident(g9,g4)
    c: Coincident(g8,g5)
    c: Coincident(g9,g6)
    c: Coincident(g2,g7)
    c: Horizontal(g9)
    c: Horizontal(g8)
    c: Vertical(g7)
    c: Horizontal(g6,g2)
    c: DistanceX(g5,g4) = 0.2
    c: Coincident(g11,g2)
    c: Coincident(g11,g6)
    c: Diameter(g10) = 0.5
    c: DistanceX(g2,g2) = 1.5
    c: Tangent(g10,g11)
    c: DistanceX(g4,g4) = 0.1
    c: DistanceX(g8,g8) = 1.5
    c: DistanceX(g9,g9) = 1
    c: Tangent(g7,g10) = 1.5708
    c: Tangent(g6,g10) = 1.5708
    c: DistanceY(g4,g4) = 0.5
    c: DistanceY(g5,g4) = 0.05
FEATURE [PartDesign::Revolution] Revolution
  Angle = 360
  Axis = (0,-2e-16,1)
  Base = (0,0,0)
  Placement = pos=(0,0,0) rot=(1,0,0;1.5708rad)
  Profile = -> Sketch035
  ReferenceAxis = -> Sketch035 [V_Axis]
  Reversed = true
FEATURE [PartDesign::Chamfer] Chamfer
  Angle = 45
  Base = -> Revolution [Edge11,Edge7]
  BaseFeature = -> Revolution
  ChamferType = 0
  FlipDirection = false
  Placement = pos=(0,0,0) rot=(1,0,0;1.5708rad)
  Size = 0.4
  Size2 = 1
  SupportTransform = false
  UseAllEdges = false
FEATURE [PartDesign::Body] Body010  label="rear bearing"
  Group = -> [Sketch035,Revolution,Chamfer]
  Origin = -> Origin011
  Placement = pos=(0,0,6.6) rot=(0,0,1;0rad)
  Tip = -> Chamfer
FEATURE [Sketcher::SketchObject] Sketch006
  AttachmentOffset = pos=(0,0,16) rot=(0,0,1;0rad)
  FullyConstrained = true
  MapMode = 5
  Placement = pos=(16,-3.6e-15,3.6e-15) rot=(0.57735,0.57735,0.57735;2.0944rad)
  Support = -> [YZ_Plane012]
  sketch-geometry (4):
    g0: LineSegment StartX=-7 StartY=3.8 StartZ=0 EndX=7 EndY=3.8 EndZ=0
    g1: LineSegment StartX=7 StartY=3.8 StartZ=0 EndX=7 EndY=3.2 EndZ=0
    g2: LineSegment StartX=7 StartY=3.2 StartZ=0 EndX=-7 EndY=3.2 EndZ=0
    g3: LineSegment StartX=-7 StartY=3.2 StartZ=0 EndX=-7 EndY=3.8 EndZ=0
  constraints (12):
    c: Coincident(g0,g1)
    c: Coincident(g1,g2)
    c: Coincident(g2,g3)
    c: Coincident(g3,g0)
    c: Horizontal(g0)
    c: Horizontal(g2)
    c: Vertical(g1)
    c: Vertical(g3)
    c: DistanceY(g1,g1) = 0.6
    c: DistanceX(g0,g0) = 14
    c: DistanceX(g-1,g0) = 7
    c: DistanceY(g-1,g1) = 3.2
FEATURE [PartDesign::Pad] Pad018  label="PCB"
  Direction = (1,-2e-16,3e-16)
  Length = 9.6
  Length2 = 10
  Placement = pos=(0,0,0) rot=(0.57735,0.57735,0.57735;2.0944rad)
  Profile = -> Sketch006
  ReferenceAxis = -> Sketch006 [N_Axis]
  Type = 0
FEATURE [Sketcher::SketchObject] Sketch036
  AttachmentOffset = pos=(0,0,16) rot=(0,0,1;0rad)
  FullyConstrained = true
  MapMode = 5
  Placement = pos=(16,-3.6e-15,3.6e-15) rot=(0.57735,0.57735,0.57735;2.0944rad)
  Support = -> [YZ_Plane012]
  sketch-geometry (11):
    g0: LineSegment StartX=7.8 StartY=8.8 StartZ=0 EndX=7.8 EndY=3.8 EndZ=0
    g1: LineSegment StartX=7.8 StartY=3.8 StartZ=0 EndX=0.5 EndY=3.8 EndZ=0
    g2: LineSegment StartX=-7.8 StartY=3.8 StartZ=0 EndX=-7.8 EndY=8.8 EndZ=0
    g3: LineSegment StartX=7.3 StartY=8.8 StartZ=0 EndX=7.3 EndY=4.2 EndZ=0
    g4: LineSegment StartX=7.3 StartY=4.2 StartZ=0 EndX=-7.3 EndY=4.2 EndZ=0
    g5: LineSegment StartX=-7.3 StartY=4.2 StartZ=0 EndX=-7.3 EndY=8.8 EndZ=0
    g6: LineSegment StartX=7.3 StartY=8.8 StartZ=0 EndX=7.8 EndY=8.8 EndZ=0
    g7: LineSegment StartX=-7.3 StartY=8.8 StartZ=0 EndX=-7.8 EndY=8.8 EndZ=0
    g8: LineSegment StartX=-0.5 StartY=3.8 StartZ=0 EndX=0 EndY=3.4 EndZ=0
    g9: LineSegment StartX=0 StartY=3.4 StartZ=0 EndX=0.5 EndY=3.8 EndZ=0
    g10: LineSegment StartX=-0.5 StartY=3.8 StartZ=0 EndX=-7.8 EndY=3.8 EndZ=0
  constraints (33):
    c: Coincident(g0,g1)
    c: Coincident(g10,g2)
    c: Horizontal(g1)
    c: Vertical(g0)
    c: Vertical(g2)
    c: Coincident(g3,g4)
    c: Coincident(g4,g5)
    c: Horizontal(g4)
    c: Vertical(g3)
    c: Vertical(g5)
    c: DistanceX(g10,g0) = 15.6
    c: DistanceX(g-1,g0) = 7.8
    c: DistanceY(g-1,g0) = 3.8
    c: DistanceY(g10,g4) = 0.4
    c: DistanceX(g2,g5) = 0.5
    c: DistanceX(g3,g0) = 0.5
    c: Horizontal(g5,g3)
    c: DistanceY(g0,g0) = 5
    c: Coincident(g6,g3)
    c: Coincident(g6,g0)
    c: Coincident(g7,g5)
    c: Coincident(g7,g2)
    c: Horizontal(g7)
    c: Horizontal(g6)
    c: PointOnObject(g8,g-2)
    c: Coincident(g9,g8)
    c: DistanceX(g8,g9) = 1
    c: DistanceX(g-1,g9) = 0.5
    c: DistanceY(g8,g9) = 0.4
    c: Coincident(g1,g9)
    c: Coincident(g10,g8)
    c: Horizontal(g8,g1)
    c: Horizontal(g10)
FEATURE [PartDesign::Pad] Pad019  label="shell"
  BaseFeature = -> Pad018
  Direction = (1,-2e-16,3e-16)
  Length = 9
  Length2 = 10
  Placement = pos=(0,0,0) rot=(0.57735,0.57735,0.57735;2.0944rad)
  Profile = -> Sketch036
  ReferenceAxis = -> Sketch036 [N_Axis]
  Type = 0
FEATURE [Sketcher::SketchObject] Sketch037
  AttachmentOffset = pos=(0,0,16) rot=(0,0,1;0rad)
  FullyConstrained = true
  MapMode = 5
  Placement = pos=(16,-3.6e-15,3.6e-15) rot=(0.57735,0.57735,0.57735;2.0944rad)
  Support = -> [YZ_Plane012]
  sketch-geometry (8):
    g0: LineSegment StartX=-7 StartY=9.4 StartZ=0 EndX=7 EndY=9.4 EndZ=0
    g1: LineSegment StartX=7 StartY=9.4 StartZ=0 EndX=7 EndY=4.2 EndZ=0
    g2: LineSegment StartX=7 StartY=4.2 StartZ=0 EndX=6.1 EndY=4.2 EndZ=0
    g3: LineSegment StartX=-7 StartY=4.2 StartZ=0 EndX=-7 EndY=9.4 EndZ=0
    g4: LineSegment StartX=-6.1 StartY=4.2 StartZ=0 EndX=-6.1 EndY=4.5 EndZ=0
    g5: LineSegment StartX=-6.1 StartY=4.5 StartZ=0 EndX=6.1 EndY=4.5 EndZ=0
    g6: LineSegment StartX=6.1 StartY=4.5 StartZ=0 EndX=6.1 EndY=4.2 EndZ=0
    g7: LineSegment StartX=-6.1 StartY=4.2 StartZ=0 EndX=-7 EndY=4.2 EndZ=0
  constraints (24):
    c: Coincident(g0,g1)
    c: Coincident(g1,g2)
    c: Coincident(g7,g3)
    c: Coincident(g3,g0)
    c: Horizontal(g0)
    c: Horizontal(g2)
    c: Vertical(g1)
    c: Vertical(g3)
    c: DistanceX(g0,g0) = 14
    c: Vertical(g4)
    c: Coincident(g5,g4)
    c: Horizontal(g5)
    c: Coincident(g6,g5)
    c: Vertical(g6)
    c: Coincident(g2,g6)
    c: Coincident(g7,g4)
    c: DistanceY(g3,g3) = 5.2
    c: Horizontal(g7)
    c: Horizontal(g4,g2)
    c: DistanceY(g-1,g4) = 4.2
    c: DistanceX(g-1,g0) = 7
    c: DistanceY(g4,g4) = 0.3
    c: DistanceX(g7,g7) = 0.9
    c: DistanceX(g2,g2) = 0.9
FEATURE [PartDesign::Pad] Pad020  label="connectorBase"
  BaseFeature = -> Pad019
  Direction = (1,-2e-16,3e-16)
  Length = 6.4
  Length2 = 10
  Placement = pos=(0,0,0) rot=(0.57735,0.57735,0.57735;2.0944rad)
  Profile = -> Sketch037
  ReferenceAxis = -> Sketch037 [N_Axis]
  Type = 0
FEATURE [Sketcher::SketchObject] Sketch038
  FullyConstrained = true
  MapMode = 5
  Placement = pos=(22.4,-4.5e-15,4e-15) rot=(0.57735,0.57735,0.57735;2.0944rad)
  Support = -> [Pad020]
  sketch-geometry (24):
    g0: LineSegment StartX=-7 StartY=9.4 StartZ=0 EndX=-4 EndY=9.4 EndZ=0
    g1: LineSegment StartX=-4 StartY=9.4 StartZ=0 EndX=-4 EndY=8.8 EndZ=0
    g2: LineSegment StartX=-4 StartY=8.8 StartZ=0 EndX=-6.4 EndY=8.8 EndZ=0
    g3: LineSegment StartX=-6.4 StartY=8.8 StartZ=0 EndX=-6.4 EndY=7.8 EndZ=0
    g4: LineSegment StartX=-6.4 StartY=7.8 StartZ=0 EndX=-7 EndY=7.8 EndZ=0
    g5: LineSegment StartX=-7 StartY=7.8 StartZ=0 EndX=-7 EndY=9.4 EndZ=0
    g6: LineSegment StartX=4 StartY=9.4 StartZ=0 EndX=7 EndY=9.4 EndZ=0
    g7: LineSegment StartX=7 StartY=9.4 StartZ=0 EndX=7 EndY=7.8 EndZ=0
    g8: LineSegment StartX=7 StartY=7.8 StartZ=0 EndX=6.4 EndY=7.8 EndZ=0
    g9: LineSegment StartX=6.4 StartY=7.8 StartZ=0 EndX=6.4 EndY=8.8 EndZ=0
    g10: LineSegment StartX=6.4 StartY=8.8 StartZ=0 EndX=4 EndY=8.8 EndZ=0
    g11: LineSegment StartX=4 StartY=8.8 StartZ=0 EndX=4 EndY=9.4 EndZ=0
    g12: LineSegment StartX=7 StartY=7 StartZ=0 EndX=7 EndY=4.2 EndZ=0
    g13: LineSegment StartX=7 StartY=4.2 StartZ=0 EndX=6.1 EndY=4.2 EndZ=0
    g14: LineSegment StartX=6.1 StartY=4.2 StartZ=0 EndX=6.1 EndY=4.5 EndZ=0
    g15: LineSegment StartX=6.1 StartY=4.5 StartZ=0 EndX=-6.1 EndY=4.5 EndZ=0
    g16: LineSegment StartX=-6.1 StartY=4.5 StartZ=0 EndX=-6.1 EndY=4.2 EndZ=0
    g17: LineSegment StartX=-6.1 StartY=4.2 StartZ=0 EndX=-7 EndY=4.2 EndZ=0
    g18: LineSegment StartX=-7 StartY=4.2 StartZ=0 EndX=-7 EndY=7 EndZ=0
    g19: LineSegment StartX=-7 StartY=7 StartZ=0 EndX=-6.4 EndY=7 EndZ=0
    g20: LineSegment StartX=-6.4 StartY=7 StartZ=0 EndX=-6.4 EndY=5.3 EndZ=0
    g21: LineSegment StartX=-6.4 StartY=5.3 StartZ=0 EndX=6.4 EndY=5.3 EndZ=0
    g22: LineSegment StartX=6.4 StartY=5.3 StartZ=0 EndX=6.4 EndY=7 EndZ=0
    g23: LineSegment StartX=6.4 StartY=7 StartZ=0 EndX=7 EndY=7 EndZ=0
  constraints (72):
    c: Horizontal(g0)
    c: Coincident(g0,g1)
    c: Coincident(g1,g2)
    c: Horizontal(g2)
    c: Coincident(g2,g3)
    c: Vertical(g3)
    c: Coincident(g3,g4)
    c: Coincident(g4,g5)
    c: Coincident(g5,g0)
    c: Vertical(g5)
    c: Horizontal(g6)
    c: Coincident(g6,g7)
    c: Vertical(g7)
    c: Coincident(g7,g8)
    c: Horizontal(g8)
    c: Coincident(g8,g9)
    c: Vertical(g9)
    c: Coincident(g9,g10)
    c: Horizontal(g10)
    c: Coincident(g10,g11)
    c: Coincident(g11,g6)
    c: Vertical(g12)
    c: Coincident(g12,g13)
    c: Coincident(g13,g14)
    c: Coincident(g14,g15)
    c: Horizontal(g15)
    c: Coincident(g15,g16)
    c: Coincident(g16,g17)
    c: Coincident(g17,g18)
    c: Vertical(g18)
    c: Coincident(g18,g19)
    c: Horizontal(g19)
    c: Coincident(g19,g20)
    c: Vertical(g20)
    c: Coincident(g20,g21)
    c: Horizontal(g21)
    c: Coincident(g21,g22)
    c: Vertical(g22)
    c: Coincident(g22,g23)
    c: Coincident(g23,g12)
    c: Vertical(g14)
    c: Vertical(g11)
    c: Vertical(g1)
    c: Vertical(g16)
    c: Horizontal(g17)
    c: Horizontal(g13)
    c: Horizontal(g23)
    c: Horizontal(g4)
    c: DistanceY(g15,g20) = 0.8
    c: DistanceX(g17,g17) = 0.9
    c: DistanceX(g13,g13) = 0.9
    c: DistanceX(g17,g12) = 14
    c: DistanceX(g-1,g12) = 7
    c: DistanceY(g16,g16) = 0.3
    c: DistanceY(g-1,g16) = 4.2
    c: Horizontal(g19,g22)
    c: DistanceX(g23,g23) = 0.6
    c: DistanceX(g19,g19) = 0.6
    c: DistanceY(g18,g18) = 2.8
    c: Horizontal(g16,g13)
    c: Vertical(g8,g22)
    c: Vertical(g19,g3)
    c: Vertical(g4,g18)
    c: Vertical(g7,g12)
    c: Horizontal(g0,g6)
    c: Horizontal(g1,g10)
    c: DistanceY(g12,g6) = 5.2
    c: DistanceY(g7,g7) = 1.6
    c: Horizontal(g3,g8)
    c: DistanceY(g1,g1) = 0.6
    c: DistanceX(g0,g6) = 8
    c: DistanceX(g-1,g6) = 4
FEATURE [PartDesign::Pad] Pad021  label="connectorShell"
  BaseFeature = -> Pad020
  Direction = (1,-7e-16,3e-16)
  Length = 4.4
  Length2 = 10
  Placement = pos=(0,0,0) rot=(0.57735,0.57735,0.57735;2.0944rad)
  Profile = -> Sketch038
  ReferenceAxis = -> Sketch038 [N_Axis]
  Type = 0
FEATURE [Sketcher::SketchObject] Sketch010
  FullyConstrained = true
  MapMode = 5
  Placement = pos=(22.4,-4.5e-15,4e-15) rot=(0.57735,0.57735,0.57735;2.0944rad)
  Support = -> [Pad021]
  sketch-geometry (24):
    g0: LineSegment StartX=-5.3 StartY=7.7 StartZ=0 EndX=-4.7 EndY=7.7 EndZ=0
    g1: LineSegment StartX=-4.7 StartY=7.7 StartZ=0 EndX=-4.7 EndY=7.1 EndZ=0
    g2: LineSegment StartX=-4.7 StartY=7.1 StartZ=0 EndX=-5.3 EndY=7.1 EndZ=0
    g3: LineSegment StartX=-5.3 StartY=7.1 StartZ=0 EndX=-5.3 EndY=7.7 EndZ=0
    g4: LineSegment StartX=-3.3 StartY=7.7 StartZ=0 EndX=-2.7 EndY=7.7 EndZ=0
    g5: LineSegment StartX=-2.7 StartY=7.7 StartZ=0 EndX=-2.7 EndY=7.1 EndZ=0
    g6: LineSegment StartX=-2.7 StartY=7.1 StartZ=0 EndX=-3.3 EndY=7.1 EndZ=0
    g7: LineSegment StartX=-3.3 StartY=7.1 StartZ=0 EndX=-3.3 EndY=7.7 EndZ=0
    g8: LineSegment StartX=-1.3 StartY=7.7 StartZ=0 EndX=-0.7 EndY=7.7 EndZ=0
    g9: LineSegment StartX=-0.7 StartY=7.7 StartZ=0 EndX=-0.7 EndY=7.1 EndZ=0
    g10: LineSegment StartX=-0.7 StartY=7.1 StartZ=0 EndX=-1.3 EndY=7.1 EndZ=0
    g11: LineSegment StartX=-1.3 StartY=7.1 StartZ=0 EndX=-1.3 EndY=7.7 EndZ=0
    g12: LineSegment StartX=0.7 StartY=7.7 StartZ=0 EndX=1.3 EndY=7.7 EndZ=0
    g13: LineSegment StartX=1.3 StartY=7.7 StartZ=0 EndX=1.3 EndY=7.1 EndZ=0
    g14: LineSegment StartX=1.3 StartY=7.1 StartZ=0 EndX=0.7 EndY=7.1 EndZ=0
    g15: LineSegment StartX=0.7 StartY=7.1 StartZ=0 EndX=0.7 EndY=7.7 EndZ=0
    g16: LineSegment StartX=2.7 StartY=7.7 StartZ=0 EndX=3.3 EndY=7.7 EndZ=0
    g17: LineSegment StartX=3.3 StartY=7.7 StartZ=0 EndX=3.3 EndY=7.1 EndZ=0
    g18: LineSegment StartX=3.3 StartY=7.1 StartZ=0 EndX=2.7 EndY=7.1 EndZ=0
    g19: LineSegment StartX=2.7 StartY=7.1 StartZ=0 EndX=2.7 EndY=7.7 EndZ=0
    g20: LineSegment StartX=4.7 StartY=7.7 StartZ=0 EndX=5.3 EndY=7.7 EndZ=0
    g21: LineSegment StartX=5.3 StartY=7.7 StartZ=0 EndX=5.3 EndY=7.1 EndZ=0
    g22: LineSegment StartX=5.3 StartY=7.1 StartZ=0 EndX=4.7 EndY=7.1 EndZ=0
    g23: LineSegment StartX=4.7 StartY=7.1 StartZ=0 EndX=4.7 EndY=7.7 EndZ=0
  constraints (72):
    c: Coincident(g0,g1)
    c: Coincident(g1,g2)
    c: Coincident(g2,g3)
    c: Coincident(g3,g0)
    c: Horizontal(g0)
    c: Horizontal(g2)
    c: Vertical(g1)
    c: Vertical(g3)
    c: Coincident(g4,g5)
    c: Coincident(g5,g6)
    c: Coincident(g6,g7)
    c: Coincident(g7,g4)
    c: Horizontal(g4)
    c: Horizontal(g6)
    c: Vertical(g5)
    c: Vertical(g7)
    c: Coincident(g8,g9)
    c: Coincident(g9,g10)
    c: Coincident(g10,g11)
    c: Coincident(g11,g8)
    c: Horizontal(g8)
    c: Horizontal(g10)
    c: Vertical(g9)
    c: Vertical(g11)
    c: Coincident(g12,g13)
    c: Coincident(g13,g14)
    c: Coincident(g14,g15)
    c: Coincident(g15,g12)
    c: Horizontal(g12)
    c: Horizontal(g14)
    c: Vertical(g13)
    c: Vertical(g15)
    c: Coincident(g16,g17)
    c: Coincident(g17,g18)
    c: Coincident(g18,g19)
    c: Coincident(g19,g16)
    c: Horizontal(g16)
    c: Horizontal(g18)
    c: Vertical(g17)
    c: Vertical(g19)
    c: Coincident(g20,g21)
    c: Coincident(g21,g22)
    c: Coincident(g22,g23)
    c: Coincident(g23,g20)
    c: Horizontal(g20)
    c: Horizontal(g22)
    c: Vertical(g21)
    c: Vertical(g23)
    c: Horizontal(g0,g4)
    c: Horizontal(g4,g8)
    c: Horizontal(g8,g12)
    c: Horizontal(g12,g16)
    c: Horizontal(g16,g20)
    c: Horizontal(g1,g6)
    c: Horizontal(g5,g10)
    c: Horizontal(g9,g14)
    c: Horizontal(g13,g18)
    c: Horizontal(g17,g22)
    c: Equal(g2,g6)
    c: Equal(g6,g10)
    c: Equal(g10,g14)
    c: Equal(g14,g18)
    c: Equal(g18,g22)
    c: DistanceX(g0,g0) = 0.6
    c: DistanceY(g3,g3) = 0.6
    c: Distance(g0,g4) = 2
    c: Distance(g4,g8) = 2
    c: Distance(g8,g12) = 2
    c: Distance(g12,g16) = 2
    c: Distance(g16,g20) = 2
    c: DistanceX(g-1,g14) = 0.7
    c: DistanceY(g-1,g14) = 7.1
FEATURE [PartDesign::Pad] Pad022  label="connectorPins"
  BaseFeature = -> Pad021
  Direction = (1,-6e-16,3e-16)
  Length = 3.5
  Length2 = 10
  Placement = pos=(0,0,0) rot=(0.57735,0.57735,0.57735;2.0944rad)
  Profile = -> Sketch010
  ReferenceAxis = -> Sketch010 [N_Axis]
  Type = 0
FEATURE [PartDesign::Body] Body011  label="connector"
  Group = -> [Sketch006,Pad018,Sketch036,Pad019,Sketch037,Pad020,Sketch038,Pad021,Sketch010,Pad022]
  Origin = -> Origin012
  Tip = -> Pad022
FEATURE [Sketcher::SketchObject] Sketch041  label="basic outline001"
  FullyConstrained = true
  MapMode = 5
  Support = -> [XY_Plane014]
  sketch-geometry (9):
    g0: ArcOfCircle CenterX=0 CenterY=0 CenterZ=0 NormalX=0 NormalY=0 NormalZ=1 AngleXU=0 Radius=25.2 StartAngle=2.15648 EndAngle=2.55591
    g1: ArcOfCircle CenterX=0 CenterY=0 CenterZ=0 NormalX=0 NormalY=0 NormalZ=1 AngleXU=0 Radius=25.2 StartAngle=5.29807 EndAngle=5.6975
    g2: ArcOfCircle CenterX=0 CenterY=0 CenterZ=0 NormalX=0 NormalY=0 NormalZ=1 AngleXU=0 Radius=25.2 StartAngle=0.585686 EndAngle=0.985111
    g3: ArcOfCircle CenterX=0 CenterY=0 CenterZ=0 NormalX=0 NormalY=0 NormalZ=1 AngleXU=0 Radius=25.2 StartAngle=3.72728 EndAngle=4.1267
    g4: LineSegment StartX=-13.9298 StartY=21 StartZ=0 EndX=13.9298 EndY=21 EndZ=0
    g5: LineSegment StartX=21 StartY=13.9298 StartZ=0 EndX=21 EndY=-13.9298 EndZ=0
    g6: LineSegment StartX=-13.9298 StartY=-21 StartZ=0 EndX=13.9298 EndY=-21 EndZ=0
    g7: LineSegment StartX=-21 StartY=13.9298 StartZ=0 EndX=-21 EndY=-13.9298 EndZ=0
    g8: Circle CenterX=0 CenterY=0 CenterZ=0 NormalX=0 NormalY=0 NormalZ=1 AngleXU=0 Radius=4.5
  constraints (26):
    c: Coincident(g0,g-1)
    c: Coincident(g1,g0)
    c: Coincident(g2,g0)
    c: Coincident(g3,g0)
    c: Equal(g0,g1)
    c: Equal(g1,g2)
    c: Equal(g2,g3)
    c: Coincident(g4,g0)
    c: Coincident(g4,g2)
    c: Horizontal(g4)
    c: Coincident(g5,g2)
    c: Coincident(g5,g1)
    c: Vertical(g5)
    c: Coincident(g6,g3)
    c: Coincident(g6,g1)
    c: Coincident(g7,g0)
    c: Coincident(g7,g3)
    c: Vertical(g7)
    c: Horizontal(g6)
    c: DistanceX(g0,g2) = 42
    c: DistanceY(g1,g2) = 42
    c: DistanceY(g0,g2) = 21
    c: DistanceX(g0,g0) = 21
    c: Coincident(g8,g0)
    c: Diameter(g8) = 9
    c: Diameter(g0) = 50.4
FEATURE [PartDesign::Pad] Pad024  label="statorLamination"
  Direction = (0,0,1)
  Length = 0.52
  Length2 = 10
  Profile = -> Sketch041
  ReferenceAxis = -> Sketch041 [N_Axis]
  Type = 0
FEATURE [PartDesign::LinearPattern] LinearPattern  label="stack"
  BaseFeature = -> Pad024
  Direction = -> Z_Axis014
  Length = 19.48
  Occurrences = 40
  Originals = -> [Pad024]
FEATURE [PartDesign::Body] Body013  label="stator"
  Group = -> [Sketch041,Pad024,LinearPattern]
  Origin = -> Origin014
  Placement = pos=(0,0,9.4) rot=(0,0,1;0rad)
  Tip = -> LinearPattern
FEATURE [Sketcher::SketchObject] Sketch045
  FullyConstrained = true
  MapMode = 5
  Placement = pos=(0,0,0) rot=(1,0,0;1.5708rad)
  Support = -> [XZ_Plane016]
  sketch-geometry (12):
    g0: LineSegment StartX=2.5 StartY=2.55 StartZ=0 EndX=8 EndY=2.55 EndZ=0
    g1: LineSegment StartX=8 StartY=2.55 StartZ=0 EndX=8 EndY=-2.45 EndZ=0
    g2: LineSegment StartX=8 StartY=-2.45 StartZ=0 EndX=6.5 EndY=-2.45 EndZ=0
    g3: LineSegment StartX=2.5 StartY=-2.5 StartZ=0 EndX=2.5 EndY=2.55 EndZ=0
    g4: LineSegment StartX=4.2 StartY=-2.45 StartZ=0 EndX=4.1 EndY=-1.95 EndZ=0
    g5: LineSegment StartX=4.1 StartY=-1.95 StartZ=0 EndX=4 EndY=-2.5 EndZ=0
    g6: LineSegment StartX=5.2 StartY=-2.45 StartZ=0 EndX=6.13734 EndY=-1.97682 EndZ=0
    g7: LineSegment StartX=6.5 StartY=-2.2 StartZ=0 EndX=6.5 EndY=-2.45 EndZ=0
    g8: LineSegment StartX=4 StartY=-2.5 StartZ=0 EndX=2.5 EndY=-2.5 EndZ=0
    g9: LineSegment StartX=5.2 StartY=-2.45 StartZ=0 EndX=4.2 EndY=-2.45 EndZ=0
    g10: ArcOfCircle CenterX=6.25 CenterY=-2.2 CenterZ=0 NormalX=0 NormalY=0 NormalZ=1 AngleXU=0 Radius=0.25 StartAngle=2.03828 EndAngle=6.28319
    g11: LineSegment StartX=6.5 StartY=-2.45 StartZ=0 EndX=5.2 EndY=-2.45 EndZ=0
  constraints (34):
    c: Coincident(g0,g1)
    c: Coincident(g1,g2)
    c: Coincident(g8,g3)
    c: Coincident(g3,g0)
    c: Horizontal(g0)
    c: Horizontal(g2)
    c: Vertical(g1)
    c: Vertical(g3)
    c: Coincident(g5,g4)
    c: DistanceX(g-1,g8) = 2.5
    c: DistanceX(g-1,g1) = 8
    c: DistanceY(g1,g1) = 5
    c: DistanceY(g8,g-1) = 2.5
    c: Coincident(g9,g4)
    c: Coincident(g8,g5)
    c: Coincident(g9,g6)
    c: Coincident(g2,g7)
    c: Horizontal(g9)
    c: Horizontal(g8)
    c: Vertical(g7)
    c: Horizontal(g6,g2)
    c: DistanceX(g5,g4) = 0.2
    c: Coincident(g11,g2)
    c: Coincident(g11,g6)
    c: Diameter(g10) = 0.5
    c: DistanceX(g2,g2) = 1.5
    c: Tangent(g10,g11)
    c: DistanceX(g4,g4) = 0.1
    c: DistanceX(g8,g8) = 1.5
    c: DistanceX(g9,g9) = 1
    c: Tangent(g7,g10) = 1.5708
    c: Tangent(g6,g10) = 1.5708
    c: DistanceY(g4,g4) = 0.5
    c: DistanceY(g5,g4) = 0.05
FEATURE [PartDesign::Revolution] Revolution001
  Angle = 360
  Axis = (0,-2e-16,1)
  Base = (0,0,0)
  Placement = pos=(0,0,0) rot=(1,0,0;1.5708rad)
  Profile = -> Sketch045
  ReferenceAxis = -> Sketch045 [V_Axis]
  Reversed = true
FEATURE [PartDesign::Chamfer] Chamfer001
  Angle = 45
  Base = -> Revolution001 [Edge11,Edge7]
  BaseFeature = -> Revolution001
  ChamferType = 0
  FlipDirection = false
  Placement = pos=(0,0,0) rot=(1,0,0;1.5708rad)
  Size = 0.4
  Size2 = 1
  SupportTransform = false
  UseAllEdges = false
FEATURE [PartDesign::Body] Body015  label="front bearing"
  Group = -> [Sketch045,Revolution001,Chamfer001]
  Origin = -> Origin016
  Placement = pos=(0,0,34.6) rot=(0,1,0;3.14159rad)
  Tip = -> Chamfer001
FEATURE [Sketcher::SketchObject] Sketch042  label="basic outline002"
  FullyConstrained = true
  MapMode = 5
  Support = -> [XY_Plane015]
  sketch-geometry (13):
    g0: ArcOfCircle CenterX=0 CenterY=0 CenterZ=0 NormalX=0 NormalY=0 NormalZ=1 AngleXU=0 Radius=26.8 StartAngle=2.24118 EndAngle=2.47121
    g1: ArcOfCircle CenterX=0 CenterY=0 CenterZ=0 NormalX=0 NormalY=0 NormalZ=1 AngleXU=0 Radius=26.8 StartAngle=5.38277 EndAngle=5.6128
    g2: ArcOfCircle CenterX=0 CenterY=0 CenterZ=0 NormalX=0 NormalY=0 NormalZ=1 AngleXU=0 Radius=26.8 StartAngle=0.670386 EndAngle=0.900411
    g3: ArcOfCircle CenterX=0 CenterY=0 CenterZ=0 NormalX=0 NormalY=0 NormalZ=1 AngleXU=0 Radius=26.8 StartAngle=3.81198 EndAngle=4.042
    g4: LineSegment StartX=-16.6505 StartY=21 StartZ=0 EndX=16.6505 EndY=21 EndZ=0
    g5: LineSegment StartX=21 StartY=16.6505 StartZ=0 EndX=21 EndY=-16.6505 EndZ=0
    g6: LineSegment StartX=-16.6505 StartY=-21 StartZ=0 EndX=16.6505 EndY=-21 EndZ=0
    g7: LineSegment StartX=-21 StartY=16.6505 StartZ=0 EndX=-21 EndY=-16.6505 EndZ=0
    g8: Circle CenterX=0 CenterY=0 CenterZ=0 NormalX=0 NormalY=0 NormalZ=1 AngleXU=0 Radius=4.5
    g9: Circle CenterX=-15.5 CenterY=15.5 CenterZ=0 NormalX=0 NormalY=0 NormalZ=1 AngleXU=0 Radius=1.5
    g10: Circle CenterX=15.5 CenterY=15.5 CenterZ=0 NormalX=0 NormalY=0 NormalZ=1 AngleXU=0 Radius=1.5
    g11: Circle CenterX=15.5 CenterY=-15.5 CenterZ=0 NormalX=0 NormalY=0 NormalZ=1 AngleXU=0 Radius=1.5
    g12: Circle CenterX=-15.5 CenterY=-15.5 CenterZ=0 NormalX=0 NormalY=0 NormalZ=1 AngleXU=0 Radius=1.5
  constraints (38):
    c: Coincident(g0,g-1)
    c: Coincident(g1,g0)
    c: Coincident(g2,g0)
    c: Coincident(g3,g0)
    c: Equal(g0,g1)
    c: Equal(g1,g2)
    c: Equal(g2,g3)
    c: Radius(g0) = 26.8
    c: Coincident(g4,g0)
    c: Coincident(g4,g2)
    c: Horizontal(g4)
    c: Coincident(g5,g2)
    c: Coincident(g5,g1)
    c: Vertical(g5)
    c: Coincident(g6,g3)
    c: Coincident(g6,g1)
    c: Coincident(g7,g0)
    c: Coincident(g7,g3)
    c: Vertical(g7)
    c: Horizontal(g6)
    c: DistanceX(g0,g2) = 42
    c: DistanceY(g1,g2) = 42
    c: DistanceY(g0,g2) = 21
    c: DistanceX(g0,g0) = 21
    c: Coincident(g8,g0)
    c: Diameter(g8) = 9
    c: Vertical(g9,g12)
    c: Vertical(g11,g10)
    c: Horizontal(g9,g10)
    c: Horizontal(g12,g11)
    c: Equal(g9,g10)
    c: Equal(g11,g10)
    c: Equal(g11,g12)
    c: Diameter(g9) = 3
    c: DistanceX(g9,g10) = 31
    c: DistanceY(g11,g10) = 31
    c: DistanceY(g0,g10) = 15.5
    c: DistanceX(g0,g10) = 15.5
FEATURE [PartDesign::Pad] Pad025
  Direction = (0,0,1)
  Length = 8
  Length2 = 10
  Profile = -> Sketch042
  ReferenceAxis = -> Sketch042 [N_Axis]
  Type = 0
FEATURE [Sketcher::SketchObject] Sketch043
  FullyConstrained = true
  MapMode = 5
  Placement = pos=(0,0,8) rot=(0,0,1;0rad)
  Support = -> [Pad025]
  sketch-geometry (2):
    g0: Circle CenterX=0 CenterY=0 CenterZ=0 NormalX=0 NormalY=0 NormalZ=1 AngleXU=0 Radius=4.5
    g1: Circle CenterX=0 CenterY=0 CenterZ=0 NormalX=0 NormalY=0 NormalZ=1 AngleXU=0 Radius=11
  constraints (4):
    c: Coincident(g0,g-1)
    c: Coincident(g1,g0)
    c: Diameter(g1) = 22
    c: Diameter(g0) = 9
FEATURE [PartDesign::Pad] Pad026  label="locating boss"
  BaseFeature = -> Pad025
  Direction = (0,0,1)
  Length = 2
  Length2 = 10
  Profile = -> Sketch043
  ReferenceAxis = -> Sketch043 [N_Axis]
  Type = 0
FEATURE [Sketcher::SketchObject] Sketch044
  FullyConstrained = true
  MapMode = 5
  Support = -> [XY_Plane015]
  sketch-geometry (1):
    g0: Circle CenterX=0 CenterY=0 CenterZ=0 NormalX=0 NormalY=0 NormalZ=1 AngleXU=0 Radius=8
  constraints (2):
    c: Coincident(g0,g-1)
    c: Diameter(g0) = 16
FEATURE [PartDesign::Pocket] Pocket004
  BaseFeature = -> Pad026
  Direction = (0,0,-1)
  Length = 8.4
  Length2 = 5
  Profile = -> Sketch044
  ReferenceAxis = -> Sketch044 [N_Axis]
  Reversed = true
  Type = 0
FEATURE [PartDesign::Chamfer] Chamfer003
  Angle = 45
  Base = -> Pocket004 [Edge42,Edge30,Edge28,Edge26,Edge27,Edge44,Edge43]
  BaseFeature = -> Pocket004
  ChamferType = 0
  FlipDirection = false
  Size = 0.2
  Size2 = 1
  SupportTransform = false
  UseAllEdges = false
FEATURE [PartDesign::Fillet] Fillet004
  Base = -> Chamfer003 [Edge17,Edge16,Edge19,Edge23,Edge29,Edge27,Edge25,Edge21]
  BaseFeature = -> Chamfer003
  Radius = 0.4
  SupportTransform = false
  UseAllEdges = false
FEATURE [PartDesign::Body] Body014  label="front end cap"
  Group = -> [Sketch042,Pad025,Sketch043,Pad026,Sketch044,Pocket004,Chamfer003,Fillet004]
  Origin = -> Origin015
  Placement = pos=(0,0,29.4) rot=(0,0,1;0rad)
  Tip = -> Fillet004
COMPONENT P15 — recipe-attached ("Part002", modeled in this document).
Construction recipe (the document's own serialized feature program — sketch geometry with constraints, then the solid features built on it; lengths are millimeters unless a unit is written):

FEATURE [Sketcher::SketchObject] Sketch057
  FullyConstrained = true
  MapMode = 5
  Placement = pos=(0,0,0) rot=(0,1,0;3.14159rad)
  Support = -> [XY_Plane023]
  sketch-geometry (1):
    g0: Circle CenterX=0 CenterY=0 CenterZ=0 NormalX=0 NormalY=0 NormalZ=1 AngleXU=0 Radius=17.5
  constraints (2):
    c: Coincident(g0,g-1)
    c: Diameter(g0) = 35
FEATURE [PartDesign::FeaturePython] TimingGear004  # WARN: FeaturePython — macro-defined, semantics opaque (R4)
  AttacherType = Attacher::AttachEngine3D
  h = 0.75
  height = 6
  num_teeth = 60
  offset = 0.4
  pitch = 2
  r0 = 0.555
  r1 = 1
  rs = 0.15
  type = 0
  u = 0.254
  version = 1.3.0
FEATURE [PartDesign::Pad] Pad034
  BaseFeature = -> TimingGear004
  Direction = (0,0,-1)
  Length = 0.5
  Length2 = 10
  Profile = -> Sketch057
  ReferenceAxis = -> Sketch057 [N_Axis]
  Refine = true
  Type = 0
FEATURE [Sketcher::SketchObject] Sketch060
  FullyConstrained = true
  MapMode = 5
  Placement = pos=(0,0,0) rot=(0,1,0;3.14159rad)
  Support = -> [XY_Plane024]
  sketch-geometry (1):
    g0: Circle CenterX=0 CenterY=0 CenterZ=0 NormalX=0 NormalY=0 NormalZ=1 AngleXU=0 Radius=17.5
  constraints (2):
    c: Coincident(g0,g-1)
    c: Diameter(g0) = 35
FEATURE [PartDesign::FeaturePython] TimingGear005  # WARN: FeaturePython — macro-defined, semantics opaque (R4)
  AttacherType = Attacher::AttachEngine3D
  h = 0.75
  height = 6
  num_teeth = 60
  offset = 0.4
  pitch = 2
  r0 = 0.555
  r1 = 1
  rs = 0.15
  type = 0
  u = 0.254
  version = 1.3.0
FEATURE [PartDesign::Pad] Pad037
  BaseFeature = -> TimingGear005
  Direction = (0,0,-1)
  Length = 0.5
  Length2 = 10
  Profile = -> Sketch060
  ReferenceAxis = -> Sketch060 [N_Axis]
  Refine = true
  Type = 0
FEATURE [PartDesign::Plane] DatumPlane
  AttachmentOffset = pos=(0,0,6) rot=(0,0,1;0rad)
  Length = 60
  MapMode = 5
  Placement = pos=(0,0,6) rot=(0,0,1;0rad)
  ResizeMode = 0
  Support = -> [XY_Plane023]
  Width = 60
FEATURE [Sketcher::SketchObject] Sketch058
  FullyConstrained = true
  MapMode = 5
  Placement = pos=(0,0,6) rot=(0,0,1;0rad)
  Support = -> [DatumPlane]
  sketch-geometry (1):
    g0: Circle CenterX=0 CenterY=0 CenterZ=0 NormalX=0 NormalY=0 NormalZ=1 AngleXU=0 Radius=17.5
  constraints (2):
    c: Coincident(g0,g-1)
    c: Diameter(g0) = 35
FEATURE [PartDesign::Pad] Pad035
  BaseFeature = -> Pad034
  Direction = (0,0,1)
  Length = 0.5
  Length2 = 10
  Profile = -> Sketch058
  ReferenceAxis = -> Sketch058 [N_Axis]
  Refine = true
  Type = 0
FEATURE [PartDesign::Plane] DatumPlane001
  AttachmentOffset = pos=(0,0,6.5) rot=(0,0,1;0rad)
  Length = 60
  MapMode = 5
  Placement = pos=(0,0,6.5) rot=(0,0,1;0rad)
  ResizeMode = 0
  Support = -> [XY_Plane023]
  Width = 60
FEATURE [Sketcher::SketchObject] Sketch059
  FullyConstrained = true
  MapMode = 5
  Placement = pos=(0,0,6.5) rot=(0,0,1;0rad)
  Support = -> [DatumPlane001]
  sketch-geometry (1):
    g0: Circle CenterX=0 CenterY=0 CenterZ=0 NormalX=0 NormalY=0 NormalZ=1 AngleXU=0 Radius=21
  constraints (2):
    c: Coincident(g0,g-1)
    c: Diameter(g0) = 42
FEATURE [PartDesign::Pad] Pad036
  BaseFeature = -> Pad035
  Direction = (0,0,1)
  Length = 2
  Length2 = 10
  Profile = -> Sketch059
  ReferenceAxis = -> Sketch059 [N_Axis]
  Refine = true
  Type = 0
FEATURE [PartDesign::Fillet] Fillet005
  Base = -> Pad036 [Edge4,Edge6,Edge1087]
  BaseFeature = -> Pad036
  Radius = 0.2
  Refine = true
  SupportTransform = false
  UseAllEdges = false
FEATURE [PartDesign::Body] Fillet005Body
  Group = -> [TimingGear004,Sketch057,Pad034,DatumPlane,Sketch058,Pad035,DatumPlane001,Sketch059,Pad036,Fillet005]
  Origin = -> Origin023
  Tip = -> Fillet005
FEATURE [PartDesign::Plane] DatumPlane002
  AttachmentOffset = pos=(0,0,6) rot=(0,0,1;0rad)
  Length = 60
  MapMode = 5
  Placement = pos=(0,0,6) rot=(0,0,1;0rad)
  ResizeMode = 0
  Support = -> [XY_Plane024]
  Width = 60
FEATURE [Sketcher::SketchObject] Sketch061
  FullyConstrained = true
  MapMode = 5
  Placement = pos=(0,0,6) rot=(0,0,1;0rad)
  Support = -> [DatumPlane002]
  sketch-geometry (1):
    g0: Circle CenterX=0 CenterY=0 CenterZ=0 NormalX=0 NormalY=0 NormalZ=1 AngleXU=0 Radius=17.5
  constraints (2):
    c: Coincident(g0,g-1)
    c: Diameter(g0) = 35
FEATURE [PartDesign::Pad] Pad038
  BaseFeature = -> Pad037
  Direction = (0,0,1)
  Length = 0.5
  Length2 = 10
  Profile = -> Sketch061
  ReferenceAxis = -> Sketch061 [N_Axis]
  Refine = true
  Type = 0
FEATURE [PartDesign::Plane] DatumPlane003
  AttachmentOffset = pos=(0,0,6.5) rot=(0,0,1;0rad)
  Length = 60
  MapMode = 5
  Placement = pos=(0,0,6.5) rot=(0,0,1;0rad)
  ResizeMode = 0
  Support = -> [XY_Plane024]
  Width = 60
FEATURE [Sketcher::SketchObject] Sketch062
  FullyConstrained = true
  MapMode = 5
  Placement = pos=(0,0,6.5) rot=(0,0,1;0rad)
  Support = -> [DatumPlane003]
  sketch-geometry (1):
    g0: Circle CenterX=0 CenterY=0 CenterZ=0 NormalX=0 NormalY=0 NormalZ=1 AngleXU=0 Radius=21
  constraints (2):
    c: Coincident(g0,g-1)
    c: Diameter(g0) = 42
FEATURE [PartDesign::Pad] Pad039
  BaseFeature = -> Pad038
  Direction = (0,0,1)
  Length = 2
  Length2 = 10
  Profile = -> Sketch062
  ReferenceAxis = -> Sketch062 [N_Axis]
  Refine = true
  Type = 0
FEATURE [PartDesign::Fillet] Fillet006
  Base = -> Pad039 [Edge4,Edge6,Edge1087]
  BaseFeature = -> Pad039
  Radius = 0.2
  Refine = true
  SupportTransform = false
  UseAllEdges = false
FEATURE [PartDesign::Body] Fillet006Body
  Group = -> [TimingGear005,Sketch060,Pad037,DatumPlane002,Sketch061,Pad038,DatumPlane003,Sketch062,Pad039,Fillet006]
  Origin = -> Origin024
  Tip = -> Fillet006
FEATURE [PartDesign::FeatureBase] BaseFeature002
  BaseFeature = -> Body006
FEATURE [PartDesign::Body] Pocket010Body
  BaseFeature = -> Body006
  Group = -> [BaseFeature002]
  Origin = -> Origin025
  Tip = -> BaseFeature002
PROVENANCE & LICENSES
A FreeCAD (.FCStd) document from a public repository crawl; recipes are the document's own serialized feature recipes (and, for linked parts, companion documents' recipes).
License: as declared in the source repository (recorded in the dataset sidecar).
